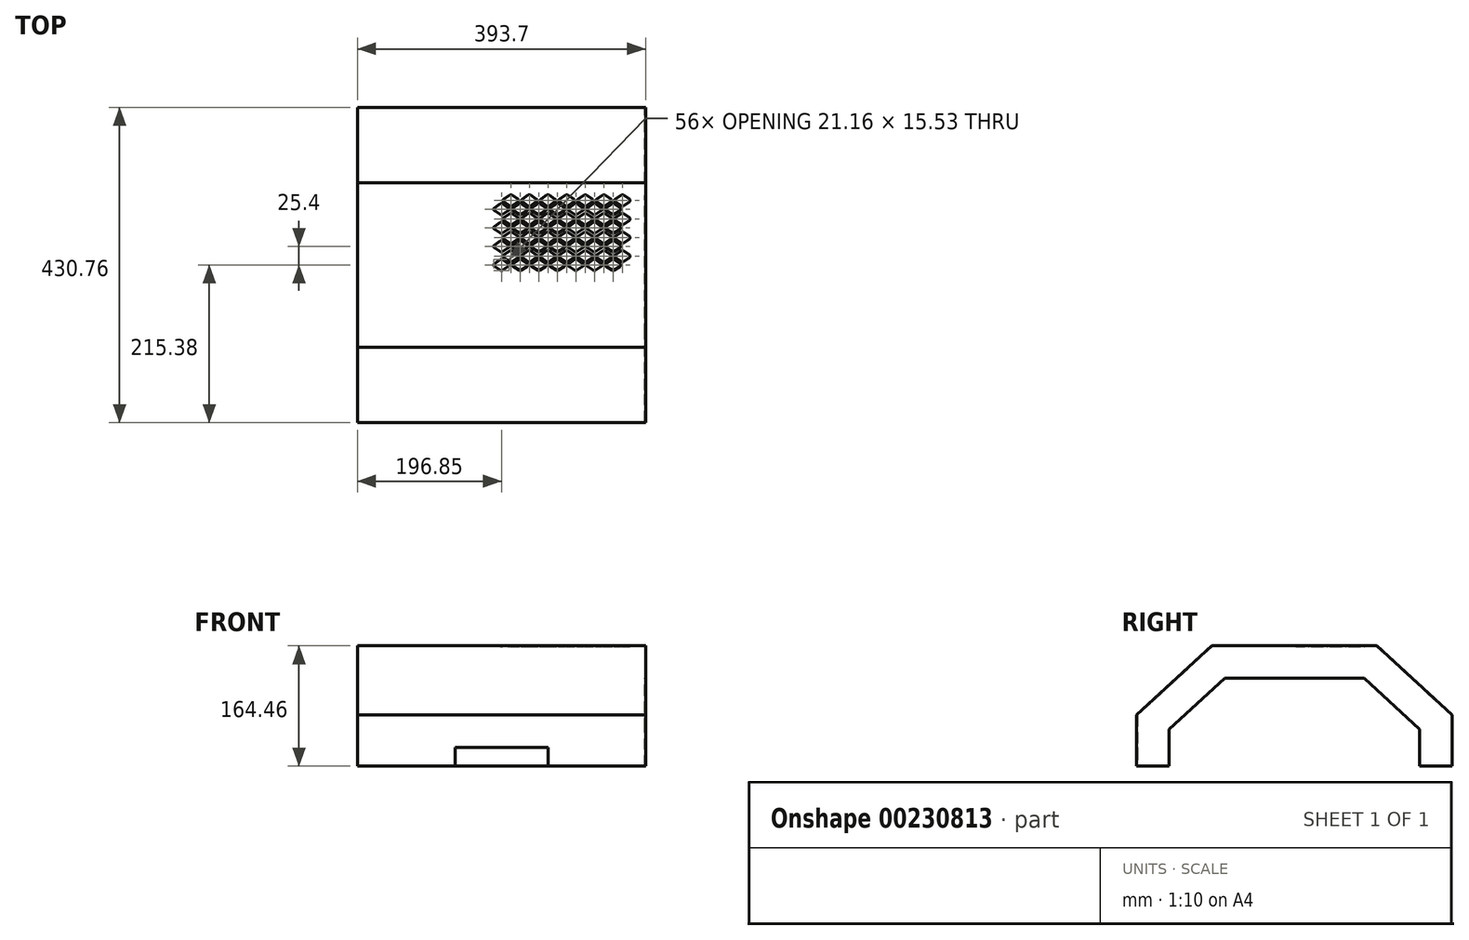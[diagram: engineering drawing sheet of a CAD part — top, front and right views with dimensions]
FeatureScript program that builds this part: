
annotation { "Feature Type Name" : "Feature", "Feature Type Description" : "" }
export const myFeature = defineFeature(function(context is Context, id is Id, definition is map)
    precondition{}
    {
        {
            var Q0;
            Q0=qCreatedBy(makeId("Right.planeOp"),FACE);
            var sketch = newSketch(context, id + "F0", { "sketchPlane" : qUnion([Q0])});
            skLineSegment(sketch, "E0", {"start": v(0, 0) * mm, "end": v(0, 169.27) * mm, "construction": true});
            skLineSegment(sketch, "E1", {"start": v(0, 164.46) * mm, "end": v(112.6, 164.46) * mm});
            skLineSegment(sketch, "E2", {"start": v(112.6, 164.46) * mm, "end": v(215.38, 69.85) * mm});
            skLineSegment(sketch, "E3", {"start": v(215.38, 69.85) * mm, "end": v(215.38, 0) * mm});
            skLineSegment(sketch, "E4", {"start": v(215.38, 0) * mm, "end": v(170.93, 0) * mm});
            skLineSegment(sketch, "E5", {"start": v(170.93, 0) * mm, "end": v(170.93, 50.35) * mm});
            skLineSegment(sketch, "E6", {"start": v(170.93, 50.35) * mm, "end": v(95.25, 120.01) * mm});
            skLineSegment(sketch, "E7", {"start": v(95.25, 120.01) * mm, "end": v(0, 120.01) * mm});
            skLineSegment(sketch, "E8.MirrorCS", {"start": v(0, 164.46) * mm, "end": v(-112.6, 164.46) * mm});
            skLineSegment(sketch, "E9.MirrorCS", {"start": v(-215.38, 0) * mm, "end": v(-170.93, 0) * mm});
            skLineSegment(sketch, "E10.MirrorCS", {"start": v(-170.93, 0) * mm, "end": v(-170.93, 50.35) * mm});
            skLineSegment(sketch, "E11.MirrorCS", {"start": v(-215.38, 69.85) * mm, "end": v(-215.38, 0) * mm});
            skLineSegment(sketch, "E12.MirrorCS", {"start": v(-95.25, 120.01) * mm, "end": v(0, 120.01) * mm});
            skLineSegment(sketch, "E13.MirrorCS", {"start": v(-112.6, 164.46) * mm, "end": v(-215.38, 69.85) * mm});
            skLineSegment(sketch, "E14.MirrorCS", {"start": v(-170.93, 50.35) * mm, "end": v(-95.25, 120.01) * mm});
            skSolve(sketch);
        }
        {
            var Q0;
            Q0=qSketchRegion(id+"F0",true);
            extrude(context, id + "F1", {"entities" : qUnion([Q0]), "endBound" : BoundingType.SYMMETRIC, "depth" : 393.7 * mm});
        }
        {
            var Q0;
            Q0=makeQuery(id+"F1.opExtrude","SWEPT_FACE",FACE,{"disambiguationData":[OSD([sQuery(id+"F0.wireOp",EDGE,"E7"),sQuery(id+"F0.wireOp",EDGE,"E12.MirrorCS")])]});
            var Q1;
            Q1=makeQuery(id+"F1.opExtrude","SWEPT_FACE",FACE,{"disambiguationData":[OSD([sQuery(id+"F0.wireOp",EDGE,"E6")])]});
            var Q2;
            Q2=makeQuery(id+"F1.opExtrude","SWEPT_FACE",FACE,{"disambiguationData":[OSD([sQuery(id+"F0.wireOp",EDGE,"E5")])]});
            var Q3;
            Q3=makeQuery(id+"F1.opExtrude","SWEPT_FACE",FACE,{"disambiguationData":[OSD([sQuery(id+"F0.wireOp",EDGE,"E4")])]});
            var Q4;
            Q4=makeQuery(id+"F1.opExtrude","SWEPT_FACE",FACE,{"disambiguationData":[OSD([sQuery(id+"F0.wireOp",EDGE,"E14.MirrorCS")])]});
            var Q5;
            Q5=makeQuery(id+"F1.opExtrude","SWEPT_FACE",FACE,{"disambiguationData":[OSD([sQuery(id+"F0.wireOp",EDGE,"E10.MirrorCS")])]});
            var Q6;
            Q6=makeQuery(id+"F1.opExtrude","SWEPT_FACE",FACE,{"disambiguationData":[OSD([sQuery(id+"F0.wireOp",EDGE,"E9.MirrorCS")])]});
            shell(context, id + "F2", {"entities" : qUnion([Q0, Q1, Q2, Q3, Q4, Q5, Q6]), "thickness" : 0.95 * mm});
        }
        {
            var Q0;
            Q0=makeQuery(id+"F1.opExtrude","SWEPT_FACE",FACE,{"disambiguationData":[OSD([sQuery(id+"F0.wireOp",EDGE,"E11.MirrorCS")])]});
            var sketch = newSketch(context, id + "F3", { "sketchPlane" : qUnion([Q0])});
            skLineSegment(sketch, "E15.bottom", {"start": v(-63.5, 0) * mm, "end": v(63.5, 0) * mm});
            skLineSegment(sketch, "E15.top", {"start": v(-63.5, 25.4) * mm, "end": v(63.5, 25.4) * mm});
            skLineSegment(sketch, "E15.left", {"start": v(-63.5, 0) * mm, "end": v(-63.5, 25.4) * mm});
            skLineSegment(sketch, "E15.right", {"start": v(63.5, 0) * mm, "end": v(63.5, 25.4) * mm});
            skSolve(sketch);
        }
        {
            var Q0;
            Q0=qSketchRegion(id+"F3",true);
            extrude(context, id + "F4", {"entities" : qUnion([Q0]), "operationType" : NewBodyOperationType.REMOVE, "oppositeDirection" : true, "depth" : 25.4 * mm});
        }
        {
            var Q0;
            Q0=makeQuery(id+"F1.opExtrude","SWEPT_FACE",FACE,{"disambiguationData":[OSD([sQuery(id+"F0.wireOp",EDGE,"E1"),sQuery(id+"F0.wireOp",EDGE,"E8.MirrorCS")])]});
            var sketch = newSketch(context, id + "F5", { "sketchPlane" : qUnion([Q0])});
            skLineSegment(sketch, "E16", {"start": v(-9.42, 2.13) * mm, "end": v(-1.38, 7.36) * mm});
            skLineSegment(sketch, "E17", {"start": v(1.38, 7.36) * mm, "end": v(9.42, 2.13) * mm});
            skLineSegment(sketch, "E18", {"start": v(9.42, -2.13) * mm, "end": v(1.38, -7.36) * mm});
            skLineSegment(sketch, "E19", {"start": v(-1.38, -7.36) * mm, "end": v(-9.42, -2.13) * mm});
            skPoint(sketch, "E20.visualSharp", {"position": v(-12.7, 0) * mm});
            skArc(sketch, "E20.filletArc", {"start": v(-9.42, 2.13) * mm, "mid": v(-10.58, 0) * mm, "end": v(-9.42, -2.13) * mm});
            skPoint(sketch, "E21.visualSharp", {"position": v(0, 8.26) * mm});
            skArc(sketch, "E21.filletArc", {"start": v(1.38, 7.36) * mm, "mid": v(0, 7.77) * mm, "end": v(-1.38, 7.36) * mm});
            skPoint(sketch, "E22.visualSharp", {"position": v(12.7, 0) * mm});
            skArc(sketch, "E22.filletArc", {"start": v(9.42, -2.13) * mm, "mid": v(10.58, 0) * mm, "end": v(9.42, 2.13) * mm});
            skPoint(sketch, "E23.visualSharp", {"position": v(0, -8.26) * mm});
            skArc(sketch, "E23.filletArc", {"start": v(-1.38, -7.36) * mm, "mid": v(0, -7.77) * mm, "end": v(1.38, -7.36) * mm});
            skLineSegment(sketch, "E24.0", {"start": v(3.28, 9.91) * mm, "end": v(11.32, 4.69) * mm});
            skLineSegment(sketch, "E25", {"start": v(3.28, 14.17) * mm, "end": v(11.32, 19.4) * mm});
            skLineSegment(sketch, "E26", {"start": v(14.08, 19.4) * mm, "end": v(22.12, 14.17) * mm});
            skLineSegment(sketch, "E27", {"start": v(22.12, 9.91) * mm, "end": v(14.08, 4.69) * mm});
            skPoint(sketch, "E28.visualSharp", {"position": v(0, 12.04) * mm});
            skArc(sketch, "E28.filletArc", {"start": v(3.28, 14.17) * mm, "mid": v(2.12, 12.04) * mm, "end": v(3.28, 9.91) * mm});
            skPoint(sketch, "E29.visualSharp", {"position": v(12.7, 20.3) * mm});
            skArc(sketch, "E29.filletArc", {"start": v(14.08, 19.4) * mm, "mid": v(12.7, 19.8) * mm, "end": v(11.32, 19.4) * mm});
            skPoint(sketch, "E30.visualSharp", {"position": v(25.4, 12.04) * mm});
            skArc(sketch, "E30.filletArc", {"start": v(22.12, 9.91) * mm, "mid": v(23.28, 12.04) * mm, "end": v(22.12, 14.17) * mm});
            skPoint(sketch, "E31.visualSharp", {"position": v(12.7, 3.79) * mm});
            skArc(sketch, "E31.filletArc", {"start": v(11.32, 4.69) * mm, "mid": v(12.7, 4.28) * mm, "end": v(14.08, 4.69) * mm});
            skPoint(sketch, "E32.0.1.0", {"position": v(25.4, 37.44) * mm});
            skPoint(sketch, "E32.0.1.1", {"position": v(12.7, 45.7) * mm});
            skPoint(sketch, "E32.0.1.2", {"position": v(0, 33.66) * mm});
            skPoint(sketch, "E32.0.1.3", {"position": v(-12.7, 25.4) * mm});
            skPoint(sketch, "E32.0.1.4", {"position": v(0, 17.14) * mm});
            skPoint(sketch, "E32.0.1.5", {"position": v(12.7, 25.4) * mm});
            skPoint(sketch, "E32.0.1.6", {"position": v(0, 37.44) * mm});
            skPoint(sketch, "E32.0.1.7", {"position": v(12.7, 29.19) * mm});
            skArc(sketch, "E32.0.1.8", {"start": v(-9.42, 27.53) * mm, "mid": v(-10.58, 25.4) * mm, "end": v(-9.42, 23.27) * mm});
            skLineSegment(sketch, "E32.0.1.9", {"start": v(14.08, 44.8) * mm, "end": v(22.12, 39.57) * mm});
            skArc(sketch, "E32.0.1.10", {"start": v(9.42, 23.27) * mm, "mid": v(10.58, 25.4) * mm, "end": v(9.42, 27.53) * mm});
            skArc(sketch, "E32.0.1.11", {"start": v(3.28, 39.57) * mm, "mid": v(2.12, 37.44) * mm, "end": v(3.28, 35.31) * mm});
            skLineSegment(sketch, "E32.0.1.12", {"start": v(3.28, 39.57) * mm, "end": v(11.32, 44.8) * mm});
            skLineSegment(sketch, "E32.0.1.13", {"start": v(9.42, 23.27) * mm, "end": v(1.38, 18.04) * mm});
            skLineSegment(sketch, "E32.0.1.14", {"start": v(-1.38, 18.04) * mm, "end": v(-9.42, 23.27) * mm});
            skLineSegment(sketch, "E32.0.1.15", {"start": v(-9.42, 27.53) * mm, "end": v(-1.38, 32.76) * mm});
            skArc(sketch, "E32.0.1.16", {"start": v(14.08, 44.8) * mm, "mid": v(12.7, 45.2) * mm, "end": v(11.32, 44.8) * mm});
            skArc(sketch, "E32.0.1.17", {"start": v(22.12, 35.31) * mm, "mid": v(23.28, 37.44) * mm, "end": v(22.12, 39.57) * mm});
            skLineSegment(sketch, "E32.0.1.18", {"start": v(22.12, 35.31) * mm, "end": v(14.08, 30.09) * mm});
            skArc(sketch, "E32.0.1.19", {"start": v(-1.38, 18.04) * mm, "mid": v(0, 17.63) * mm, "end": v(1.38, 18.04) * mm});
            skArc(sketch, "E32.0.1.20", {"start": v(1.38, 32.76) * mm, "mid": v(0, 33.17) * mm, "end": v(-1.38, 32.76) * mm});
            skLineSegment(sketch, "E32.0.1.21", {"start": v(3.28, 35.31) * mm, "end": v(11.32, 30.09) * mm});
            skLineSegment(sketch, "E32.0.1.22", {"start": v(1.38, 32.76) * mm, "end": v(9.42, 27.53) * mm});
            skArc(sketch, "E32.0.1.23", {"start": v(11.32, 30.09) * mm, "mid": v(12.7, 29.68) * mm, "end": v(14.08, 30.09) * mm});
            skPoint(sketch, "E32.0.2.0", {"position": v(25.4, 62.84) * mm});
            skPoint(sketch, "E32.0.2.1", {"position": v(12.7, 71.1) * mm});
            skPoint(sketch, "E32.0.2.2", {"position": v(0, 59.06) * mm});
            skPoint(sketch, "E32.0.2.3", {"position": v(-12.7, 50.8) * mm});
            skPoint(sketch, "E32.0.2.4", {"position": v(0, 42.55) * mm});
            skPoint(sketch, "E32.0.2.5", {"position": v(12.7, 50.8) * mm});
            skPoint(sketch, "E32.0.2.6", {"position": v(0, 62.84) * mm});
            skPoint(sketch, "E32.0.2.7", {"position": v(12.7, 54.59) * mm});
            skArc(sketch, "E32.0.2.8", {"start": v(-9.42, 52.93) * mm, "mid": v(-10.58, 50.8) * mm, "end": v(-9.42, 48.67) * mm});
            skLineSegment(sketch, "E32.0.2.9", {"start": v(14.08, 70.2) * mm, "end": v(22.12, 64.97) * mm});
            skArc(sketch, "E32.0.2.10", {"start": v(9.42, 48.67) * mm, "mid": v(10.58, 50.8) * mm, "end": v(9.42, 52.93) * mm});
            skArc(sketch, "E32.0.2.11", {"start": v(3.28, 64.97) * mm, "mid": v(2.12, 62.84) * mm, "end": v(3.28, 60.71) * mm});
            skLineSegment(sketch, "E32.0.2.12", {"start": v(3.28, 64.97) * mm, "end": v(11.32, 70.2) * mm});
            skLineSegment(sketch, "E32.0.2.13", {"start": v(9.42, 48.67) * mm, "end": v(1.38, 43.44) * mm});
            skLineSegment(sketch, "E32.0.2.14", {"start": v(-1.38, 43.44) * mm, "end": v(-9.42, 48.67) * mm});
            skLineSegment(sketch, "E32.0.2.15", {"start": v(-9.42, 52.93) * mm, "end": v(-1.38, 58.16) * mm});
            skArc(sketch, "E32.0.2.16", {"start": v(14.08, 70.2) * mm, "mid": v(12.7, 70.6) * mm, "end": v(11.32, 70.2) * mm});
            skArc(sketch, "E32.0.2.17", {"start": v(22.12, 60.71) * mm, "mid": v(23.28, 62.84) * mm, "end": v(22.12, 64.97) * mm});
            skLineSegment(sketch, "E32.0.2.18", {"start": v(22.12, 60.71) * mm, "end": v(14.08, 55.49) * mm});
            skArc(sketch, "E32.0.2.19", {"start": v(-1.38, 43.44) * mm, "mid": v(0, 43.03) * mm, "end": v(1.38, 43.44) * mm});
            skArc(sketch, "E32.0.2.20", {"start": v(1.38, 58.16) * mm, "mid": v(0, 58.57) * mm, "end": v(-1.38, 58.16) * mm});
            skLineSegment(sketch, "E32.0.2.21", {"start": v(3.28, 60.71) * mm, "end": v(11.32, 55.49) * mm});
            skLineSegment(sketch, "E32.0.2.22", {"start": v(1.38, 58.16) * mm, "end": v(9.42, 52.93) * mm});
            skArc(sketch, "E32.0.2.23", {"start": v(11.32, 55.49) * mm, "mid": v(12.7, 55.08) * mm, "end": v(14.08, 55.49) * mm});
            skPoint(sketch, "E32.0.3.0", {"position": v(25.4, 88.24) * mm});
            skPoint(sketch, "E32.0.3.1", {"position": v(12.7, 96.5) * mm});
            skPoint(sketch, "E32.0.3.2", {"position": v(0, 84.45) * mm});
            skPoint(sketch, "E32.0.3.3", {"position": v(-12.7, 76.2) * mm});
            skPoint(sketch, "E32.0.3.4", {"position": v(0, 67.94) * mm});
            skPoint(sketch, "E32.0.3.5", {"position": v(12.7, 76.2) * mm});
            skPoint(sketch, "E32.0.3.6", {"position": v(0, 88.24) * mm});
            skPoint(sketch, "E32.0.3.7", {"position": v(12.7, 79.99) * mm});
            skArc(sketch, "E32.0.3.8", {"start": v(-9.42, 78.33) * mm, "mid": v(-10.58, 76.2) * mm, "end": v(-9.42, 74.07) * mm});
            skLineSegment(sketch, "E32.0.3.9", {"start": v(14.08, 95.6) * mm, "end": v(22.12, 90.37) * mm});
            skArc(sketch, "E32.0.3.10", {"start": v(9.42, 74.07) * mm, "mid": v(10.58, 76.2) * mm, "end": v(9.42, 78.33) * mm});
            skArc(sketch, "E32.0.3.11", {"start": v(3.28, 90.37) * mm, "mid": v(2.12, 88.24) * mm, "end": v(3.28, 86.11) * mm});
            skLineSegment(sketch, "E32.0.3.12", {"start": v(3.28, 90.37) * mm, "end": v(11.32, 95.6) * mm});
            skLineSegment(sketch, "E32.0.3.13", {"start": v(9.42, 74.07) * mm, "end": v(1.38, 68.84) * mm});
            skLineSegment(sketch, "E32.0.3.14", {"start": v(-1.38, 68.84) * mm, "end": v(-9.42, 74.07) * mm});
            skLineSegment(sketch, "E32.0.3.15", {"start": v(-9.42, 78.33) * mm, "end": v(-1.38, 83.56) * mm});
            skArc(sketch, "E32.0.3.16", {"start": v(14.08, 95.6) * mm, "mid": v(12.7, 96) * mm, "end": v(11.32, 95.6) * mm});
            skArc(sketch, "E32.0.3.17", {"start": v(22.12, 86.11) * mm, "mid": v(23.28, 88.24) * mm, "end": v(22.12, 90.37) * mm});
            skLineSegment(sketch, "E32.0.3.18", {"start": v(22.12, 86.11) * mm, "end": v(14.08, 80.89) * mm});
            skArc(sketch, "E32.0.3.19", {"start": v(-1.38, 68.84) * mm, "mid": v(0, 68.43) * mm, "end": v(1.38, 68.84) * mm});
            skArc(sketch, "E32.0.3.20", {"start": v(1.38, 83.56) * mm, "mid": v(0, 83.97) * mm, "end": v(-1.38, 83.56) * mm});
            skLineSegment(sketch, "E32.0.3.21", {"start": v(3.28, 86.11) * mm, "end": v(11.32, 80.89) * mm});
            skLineSegment(sketch, "E32.0.3.22", {"start": v(1.38, 83.56) * mm, "end": v(9.42, 78.33) * mm});
            skArc(sketch, "E32.0.3.23", {"start": v(11.32, 80.89) * mm, "mid": v(12.7, 80.48) * mm, "end": v(14.08, 80.89) * mm});
            skPoint(sketch, "E32.1.0.0", {"position": v(50.8, 12.04) * mm});
            skPoint(sketch, "E32.1.0.1", {"position": v(38.1, 20.3) * mm});
            skPoint(sketch, "E32.1.0.2", {"position": v(25.4, 8.26) * mm});
            skPoint(sketch, "E32.1.0.4", {"position": v(25.4, -8.26) * mm});
            skPoint(sketch, "E32.1.0.5", {"position": v(38.1, 0) * mm});
            skPoint(sketch, "E32.1.0.7", {"position": v(38.1, 3.79) * mm});
            skArc(sketch, "E32.1.0.8", {"start": v(15.98, 2.13) * mm, "mid": v(14.82, 0) * mm, "end": v(15.98, -2.13) * mm});
            skLineSegment(sketch, "E32.1.0.9", {"start": v(39.48, 19.4) * mm, "end": v(47.52, 14.17) * mm});
            skArc(sketch, "E32.1.0.10", {"start": v(34.82, -2.13) * mm, "mid": v(35.98, 0) * mm, "end": v(34.82, 2.13) * mm});
            skArc(sketch, "E32.1.0.11", {"start": v(28.68, 14.17) * mm, "mid": v(27.52, 12.04) * mm, "end": v(28.68, 9.91) * mm});
            skLineSegment(sketch, "E32.1.0.12", {"start": v(28.68, 14.17) * mm, "end": v(36.72, 19.4) * mm});
            skLineSegment(sketch, "E32.1.0.13", {"start": v(34.82, -2.13) * mm, "end": v(26.78, -7.36) * mm});
            skLineSegment(sketch, "E32.1.0.14", {"start": v(24.02, -7.36) * mm, "end": v(15.98, -2.13) * mm});
            skLineSegment(sketch, "E32.1.0.15", {"start": v(15.98, 2.13) * mm, "end": v(24.02, 7.36) * mm});
            skArc(sketch, "E32.1.0.16", {"start": v(39.48, 19.4) * mm, "mid": v(38.1, 19.8) * mm, "end": v(36.72, 19.4) * mm});
            skArc(sketch, "E32.1.0.17", {"start": v(47.52, 9.91) * mm, "mid": v(48.68, 12.04) * mm, "end": v(47.52, 14.17) * mm});
            skLineSegment(sketch, "E32.1.0.18", {"start": v(47.52, 9.91) * mm, "end": v(39.48, 4.69) * mm});
            skArc(sketch, "E32.1.0.19", {"start": v(24.02, -7.36) * mm, "mid": v(25.4, -7.77) * mm, "end": v(26.78, -7.36) * mm});
            skArc(sketch, "E32.1.0.20", {"start": v(26.78, 7.36) * mm, "mid": v(25.4, 7.77) * mm, "end": v(24.02, 7.36) * mm});
            skLineSegment(sketch, "E32.1.0.21", {"start": v(28.68, 9.91) * mm, "end": v(36.72, 4.69) * mm});
            skLineSegment(sketch, "E32.1.0.22", {"start": v(26.78, 7.36) * mm, "end": v(34.82, 2.13) * mm});
            skArc(sketch, "E32.1.0.23", {"start": v(36.72, 4.69) * mm, "mid": v(38.1, 4.28) * mm, "end": v(39.48, 4.69) * mm});
            skPoint(sketch, "E32.1.1.0", {"position": v(50.8, 37.44) * mm});
            skPoint(sketch, "E32.1.1.1", {"position": v(38.1, 45.7) * mm});
            skPoint(sketch, "E32.1.1.2", {"position": v(25.4, 33.66) * mm});
            skPoint(sketch, "E32.1.1.3", {"position": v(12.7, 25.4) * mm});
            skPoint(sketch, "E32.1.1.4", {"position": v(25.4, 17.14) * mm});
            skPoint(sketch, "E32.1.1.5", {"position": v(38.1, 25.4) * mm});
            skPoint(sketch, "E32.1.1.6", {"position": v(25.4, 37.44) * mm});
            skPoint(sketch, "E32.1.1.7", {"position": v(38.1, 29.19) * mm});
            skArc(sketch, "E32.1.1.8", {"start": v(15.98, 27.53) * mm, "mid": v(14.82, 25.4) * mm, "end": v(15.98, 23.27) * mm});
            skLineSegment(sketch, "E32.1.1.9", {"start": v(39.48, 44.8) * mm, "end": v(47.52, 39.57) * mm});
            skArc(sketch, "E32.1.1.10", {"start": v(34.82, 23.27) * mm, "mid": v(35.98, 25.4) * mm, "end": v(34.82, 27.53) * mm});
            skArc(sketch, "E32.1.1.11", {"start": v(28.68, 39.57) * mm, "mid": v(27.52, 37.44) * mm, "end": v(28.68, 35.31) * mm});
            skLineSegment(sketch, "E32.1.1.12", {"start": v(28.68, 39.57) * mm, "end": v(36.72, 44.8) * mm});
            skLineSegment(sketch, "E32.1.1.13", {"start": v(34.82, 23.27) * mm, "end": v(26.78, 18.04) * mm});
            skLineSegment(sketch, "E32.1.1.14", {"start": v(24.02, 18.04) * mm, "end": v(15.98, 23.27) * mm});
            skLineSegment(sketch, "E32.1.1.15", {"start": v(15.98, 27.53) * mm, "end": v(24.02, 32.76) * mm});
            skArc(sketch, "E32.1.1.16", {"start": v(39.48, 44.8) * mm, "mid": v(38.1, 45.2) * mm, "end": v(36.72, 44.8) * mm});
            skArc(sketch, "E32.1.1.17", {"start": v(47.52, 35.31) * mm, "mid": v(48.68, 37.44) * mm, "end": v(47.52, 39.57) * mm});
            skLineSegment(sketch, "E32.1.1.18", {"start": v(47.52, 35.31) * mm, "end": v(39.48, 30.09) * mm});
            skArc(sketch, "E32.1.1.19", {"start": v(24.02, 18.04) * mm, "mid": v(25.4, 17.63) * mm, "end": v(26.78, 18.04) * mm});
            skArc(sketch, "E32.1.1.20", {"start": v(26.78, 32.76) * mm, "mid": v(25.4, 33.17) * mm, "end": v(24.02, 32.76) * mm});
            skLineSegment(sketch, "E32.1.1.21", {"start": v(28.68, 35.31) * mm, "end": v(36.72, 30.09) * mm});
            skLineSegment(sketch, "E32.1.1.22", {"start": v(26.78, 32.76) * mm, "end": v(34.82, 27.53) * mm});
            skArc(sketch, "E32.1.1.23", {"start": v(36.72, 30.09) * mm, "mid": v(38.1, 29.68) * mm, "end": v(39.48, 30.09) * mm});
            skPoint(sketch, "E32.1.2.0", {"position": v(50.8, 62.84) * mm});
            skPoint(sketch, "E32.1.2.1", {"position": v(38.1, 71.1) * mm});
            skPoint(sketch, "E32.1.2.2", {"position": v(25.4, 59.06) * mm});
            skPoint(sketch, "E32.1.2.3", {"position": v(12.7, 50.8) * mm});
            skPoint(sketch, "E32.1.2.4", {"position": v(25.4, 42.55) * mm});
            skPoint(sketch, "E32.1.2.5", {"position": v(38.1, 50.8) * mm});
            skPoint(sketch, "E32.1.2.6", {"position": v(25.4, 62.84) * mm});
            skPoint(sketch, "E32.1.2.7", {"position": v(38.1, 54.59) * mm});
            skArc(sketch, "E32.1.2.8", {"start": v(15.98, 52.93) * mm, "mid": v(14.82, 50.8) * mm, "end": v(15.98, 48.67) * mm});
            skLineSegment(sketch, "E32.1.2.9", {"start": v(39.48, 70.2) * mm, "end": v(47.52, 64.97) * mm});
            skArc(sketch, "E32.1.2.10", {"start": v(34.82, 48.67) * mm, "mid": v(35.98, 50.8) * mm, "end": v(34.82, 52.93) * mm});
            skArc(sketch, "E32.1.2.11", {"start": v(28.68, 64.97) * mm, "mid": v(27.52, 62.84) * mm, "end": v(28.68, 60.71) * mm});
            skLineSegment(sketch, "E32.1.2.12", {"start": v(28.68, 64.97) * mm, "end": v(36.72, 70.2) * mm});
            skLineSegment(sketch, "E32.1.2.13", {"start": v(34.82, 48.67) * mm, "end": v(26.78, 43.44) * mm});
            skLineSegment(sketch, "E32.1.2.14", {"start": v(24.02, 43.44) * mm, "end": v(15.98, 48.67) * mm});
            skLineSegment(sketch, "E32.1.2.15", {"start": v(15.98, 52.93) * mm, "end": v(24.02, 58.16) * mm});
            skArc(sketch, "E32.1.2.16", {"start": v(39.48, 70.2) * mm, "mid": v(38.1, 70.6) * mm, "end": v(36.72, 70.2) * mm});
            skArc(sketch, "E32.1.2.17", {"start": v(47.52, 60.71) * mm, "mid": v(48.68, 62.84) * mm, "end": v(47.52, 64.97) * mm});
            skLineSegment(sketch, "E32.1.2.18", {"start": v(47.52, 60.71) * mm, "end": v(39.48, 55.49) * mm});
            skArc(sketch, "E32.1.2.19", {"start": v(24.02, 43.44) * mm, "mid": v(25.4, 43.03) * mm, "end": v(26.78, 43.44) * mm});
            skArc(sketch, "E32.1.2.20", {"start": v(26.78, 58.16) * mm, "mid": v(25.4, 58.57) * mm, "end": v(24.02, 58.16) * mm});
            skLineSegment(sketch, "E32.1.2.21", {"start": v(28.68, 60.71) * mm, "end": v(36.72, 55.49) * mm});
            skLineSegment(sketch, "E32.1.2.22", {"start": v(26.78, 58.16) * mm, "end": v(34.82, 52.93) * mm});
            skArc(sketch, "E32.1.2.23", {"start": v(36.72, 55.49) * mm, "mid": v(38.1, 55.08) * mm, "end": v(39.48, 55.49) * mm});
            skPoint(sketch, "E32.1.3.0", {"position": v(50.8, 88.24) * mm});
            skPoint(sketch, "E32.1.3.1", {"position": v(38.1, 96.5) * mm});
            skPoint(sketch, "E32.1.3.2", {"position": v(25.4, 84.45) * mm});
            skPoint(sketch, "E32.1.3.3", {"position": v(12.7, 76.2) * mm});
            skPoint(sketch, "E32.1.3.4", {"position": v(25.4, 67.94) * mm});
            skPoint(sketch, "E32.1.3.5", {"position": v(38.1, 76.2) * mm});
            skPoint(sketch, "E32.1.3.6", {"position": v(25.4, 88.24) * mm});
            skPoint(sketch, "E32.1.3.7", {"position": v(38.1, 79.99) * mm});
            skArc(sketch, "E32.1.3.8", {"start": v(15.98, 78.33) * mm, "mid": v(14.82, 76.2) * mm, "end": v(15.98, 74.07) * mm});
            skLineSegment(sketch, "E32.1.3.9", {"start": v(39.48, 95.6) * mm, "end": v(47.52, 90.37) * mm});
            skArc(sketch, "E32.1.3.10", {"start": v(34.82, 74.07) * mm, "mid": v(35.98, 76.2) * mm, "end": v(34.82, 78.33) * mm});
            skArc(sketch, "E32.1.3.11", {"start": v(28.68, 90.37) * mm, "mid": v(27.52, 88.24) * mm, "end": v(28.68, 86.11) * mm});
            skLineSegment(sketch, "E32.1.3.12", {"start": v(28.68, 90.37) * mm, "end": v(36.72, 95.6) * mm});
            skLineSegment(sketch, "E32.1.3.13", {"start": v(34.82, 74.07) * mm, "end": v(26.78, 68.84) * mm});
            skLineSegment(sketch, "E32.1.3.14", {"start": v(24.02, 68.84) * mm, "end": v(15.98, 74.07) * mm});
            skLineSegment(sketch, "E32.1.3.15", {"start": v(15.98, 78.33) * mm, "end": v(24.02, 83.56) * mm});
            skArc(sketch, "E32.1.3.16", {"start": v(39.48, 95.6) * mm, "mid": v(38.1, 96) * mm, "end": v(36.72, 95.6) * mm});
            skArc(sketch, "E32.1.3.17", {"start": v(47.52, 86.11) * mm, "mid": v(48.68, 88.24) * mm, "end": v(47.52, 90.37) * mm});
            skLineSegment(sketch, "E32.1.3.18", {"start": v(47.52, 86.11) * mm, "end": v(39.48, 80.89) * mm});
            skArc(sketch, "E32.1.3.19", {"start": v(24.02, 68.84) * mm, "mid": v(25.4, 68.43) * mm, "end": v(26.78, 68.84) * mm});
            skArc(sketch, "E32.1.3.20", {"start": v(26.78, 83.56) * mm, "mid": v(25.4, 83.97) * mm, "end": v(24.02, 83.56) * mm});
            skLineSegment(sketch, "E32.1.3.21", {"start": v(28.68, 86.11) * mm, "end": v(36.72, 80.89) * mm});
            skLineSegment(sketch, "E32.1.3.22", {"start": v(26.78, 83.56) * mm, "end": v(34.82, 78.33) * mm});
            skArc(sketch, "E32.1.3.23", {"start": v(36.72, 80.89) * mm, "mid": v(38.1, 80.48) * mm, "end": v(39.48, 80.89) * mm});
            skPoint(sketch, "E32.2.0.0", {"position": v(76.2, 12.04) * mm});
            skPoint(sketch, "E32.2.0.1", {"position": v(63.5, 20.3) * mm});
            skPoint(sketch, "E32.2.0.2", {"position": v(50.8, 8.26) * mm});
            skPoint(sketch, "E32.2.0.3", {"position": v(38.1, 0) * mm});
            skPoint(sketch, "E32.2.0.4", {"position": v(50.8, -8.26) * mm});
            skPoint(sketch, "E32.2.0.5", {"position": v(63.5, 0) * mm});
            skPoint(sketch, "E32.2.0.6", {"position": v(50.8, 12.04) * mm});
            skPoint(sketch, "E32.2.0.7", {"position": v(63.5, 3.79) * mm});
            skArc(sketch, "E32.2.0.8", {"start": v(41.38, 2.13) * mm, "mid": v(40.22, 0) * mm, "end": v(41.38, -2.13) * mm});
            skLineSegment(sketch, "E32.2.0.9", {"start": v(64.88, 19.4) * mm, "end": v(72.92, 14.17) * mm});
            skArc(sketch, "E32.2.0.10", {"start": v(60.22, -2.13) * mm, "mid": v(61.38, 0) * mm, "end": v(60.22, 2.13) * mm});
            skArc(sketch, "E32.2.0.11", {"start": v(54.08, 14.17) * mm, "mid": v(52.92, 12.04) * mm, "end": v(54.08, 9.91) * mm});
            skLineSegment(sketch, "E32.2.0.12", {"start": v(54.08, 14.17) * mm, "end": v(62.12, 19.4) * mm});
            skLineSegment(sketch, "E32.2.0.13", {"start": v(60.22, -2.13) * mm, "end": v(52.18, -7.36) * mm});
            skLineSegment(sketch, "E32.2.0.14", {"start": v(49.42, -7.36) * mm, "end": v(41.38, -2.13) * mm});
            skLineSegment(sketch, "E32.2.0.15", {"start": v(41.38, 2.13) * mm, "end": v(49.42, 7.36) * mm});
            skArc(sketch, "E32.2.0.16", {"start": v(64.88, 19.4) * mm, "mid": v(63.5, 19.8) * mm, "end": v(62.12, 19.4) * mm});
            skArc(sketch, "E32.2.0.17", {"start": v(72.92, 9.91) * mm, "mid": v(74.08, 12.04) * mm, "end": v(72.92, 14.17) * mm});
            skLineSegment(sketch, "E32.2.0.18", {"start": v(72.92, 9.91) * mm, "end": v(64.88, 4.69) * mm});
            skArc(sketch, "E32.2.0.19", {"start": v(49.42, -7.36) * mm, "mid": v(50.8, -7.77) * mm, "end": v(52.18, -7.36) * mm});
            skArc(sketch, "E32.2.0.20", {"start": v(52.18, 7.36) * mm, "mid": v(50.8, 7.77) * mm, "end": v(49.42, 7.36) * mm});
            skLineSegment(sketch, "E32.2.0.21", {"start": v(54.08, 9.91) * mm, "end": v(62.12, 4.69) * mm});
            skLineSegment(sketch, "E32.2.0.22", {"start": v(52.18, 7.36) * mm, "end": v(60.22, 2.13) * mm});
            skArc(sketch, "E32.2.0.23", {"start": v(62.12, 4.69) * mm, "mid": v(63.5, 4.28) * mm, "end": v(64.88, 4.69) * mm});
            skPoint(sketch, "E32.2.1.0", {"position": v(76.2, 37.44) * mm});
            skPoint(sketch, "E32.2.1.1", {"position": v(63.5, 45.7) * mm});
            skPoint(sketch, "E32.2.1.2", {"position": v(50.8, 33.66) * mm});
            skPoint(sketch, "E32.2.1.3", {"position": v(38.1, 25.4) * mm});
            skPoint(sketch, "E32.2.1.4", {"position": v(50.8, 17.14) * mm});
            skPoint(sketch, "E32.2.1.5", {"position": v(63.5, 25.4) * mm});
            skPoint(sketch, "E32.2.1.6", {"position": v(50.8, 37.44) * mm});
            skPoint(sketch, "E32.2.1.7", {"position": v(63.5, 29.19) * mm});
            skArc(sketch, "E32.2.1.8", {"start": v(41.38, 27.53) * mm, "mid": v(40.22, 25.4) * mm, "end": v(41.38, 23.27) * mm});
            skLineSegment(sketch, "E32.2.1.9", {"start": v(64.88, 44.8) * mm, "end": v(72.92, 39.57) * mm});
            skArc(sketch, "E32.2.1.10", {"start": v(60.22, 23.27) * mm, "mid": v(61.38, 25.4) * mm, "end": v(60.22, 27.53) * mm});
            skArc(sketch, "E32.2.1.11", {"start": v(54.08, 39.57) * mm, "mid": v(52.92, 37.44) * mm, "end": v(54.08, 35.31) * mm});
            skLineSegment(sketch, "E32.2.1.12", {"start": v(54.08, 39.57) * mm, "end": v(62.12, 44.8) * mm});
            skLineSegment(sketch, "E32.2.1.13", {"start": v(60.22, 23.27) * mm, "end": v(52.18, 18.04) * mm});
            skLineSegment(sketch, "E32.2.1.14", {"start": v(49.42, 18.04) * mm, "end": v(41.38, 23.27) * mm});
            skLineSegment(sketch, "E32.2.1.15", {"start": v(41.38, 27.53) * mm, "end": v(49.42, 32.76) * mm});
            skArc(sketch, "E32.2.1.16", {"start": v(64.88, 44.8) * mm, "mid": v(63.5, 45.2) * mm, "end": v(62.12, 44.8) * mm});
            skArc(sketch, "E32.2.1.17", {"start": v(72.92, 35.31) * mm, "mid": v(74.08, 37.44) * mm, "end": v(72.92, 39.57) * mm});
            skLineSegment(sketch, "E32.2.1.18", {"start": v(72.92, 35.31) * mm, "end": v(64.88, 30.09) * mm});
            skArc(sketch, "E32.2.1.19", {"start": v(49.42, 18.04) * mm, "mid": v(50.8, 17.63) * mm, "end": v(52.18, 18.04) * mm});
            skArc(sketch, "E32.2.1.20", {"start": v(52.18, 32.76) * mm, "mid": v(50.8, 33.17) * mm, "end": v(49.42, 32.76) * mm});
            skLineSegment(sketch, "E32.2.1.21", {"start": v(54.08, 35.31) * mm, "end": v(62.12, 30.09) * mm});
            skLineSegment(sketch, "E32.2.1.22", {"start": v(52.18, 32.76) * mm, "end": v(60.22, 27.53) * mm});
            skArc(sketch, "E32.2.1.23", {"start": v(62.12, 30.09) * mm, "mid": v(63.5, 29.68) * mm, "end": v(64.88, 30.09) * mm});
            skPoint(sketch, "E32.2.2.0", {"position": v(76.2, 62.84) * mm});
            skPoint(sketch, "E32.2.2.1", {"position": v(63.5, 71.1) * mm});
            skPoint(sketch, "E32.2.2.2", {"position": v(50.8, 59.06) * mm});
            skPoint(sketch, "E32.2.2.3", {"position": v(38.1, 50.8) * mm});
            skPoint(sketch, "E32.2.2.4", {"position": v(50.8, 42.55) * mm});
            skPoint(sketch, "E32.2.2.5", {"position": v(63.5, 50.8) * mm});
            skPoint(sketch, "E32.2.2.6", {"position": v(50.8, 62.84) * mm});
            skPoint(sketch, "E32.2.2.7", {"position": v(63.5, 54.59) * mm});
            skArc(sketch, "E32.2.2.8", {"start": v(41.38, 52.93) * mm, "mid": v(40.22, 50.8) * mm, "end": v(41.38, 48.67) * mm});
            skLineSegment(sketch, "E32.2.2.9", {"start": v(64.88, 70.2) * mm, "end": v(72.92, 64.97) * mm});
            skArc(sketch, "E32.2.2.10", {"start": v(60.22, 48.67) * mm, "mid": v(61.38, 50.8) * mm, "end": v(60.22, 52.93) * mm});
            skArc(sketch, "E32.2.2.11", {"start": v(54.08, 64.97) * mm, "mid": v(52.92, 62.84) * mm, "end": v(54.08, 60.71) * mm});
            skLineSegment(sketch, "E32.2.2.12", {"start": v(54.08, 64.97) * mm, "end": v(62.12, 70.2) * mm});
            skLineSegment(sketch, "E32.2.2.13", {"start": v(60.22, 48.67) * mm, "end": v(52.18, 43.44) * mm});
            skLineSegment(sketch, "E32.2.2.14", {"start": v(49.42, 43.44) * mm, "end": v(41.38, 48.67) * mm});
            skLineSegment(sketch, "E32.2.2.15", {"start": v(41.38, 52.93) * mm, "end": v(49.42, 58.16) * mm});
            skArc(sketch, "E32.2.2.16", {"start": v(64.88, 70.2) * mm, "mid": v(63.5, 70.6) * mm, "end": v(62.12, 70.2) * mm});
            skArc(sketch, "E32.2.2.17", {"start": v(72.92, 60.71) * mm, "mid": v(74.08, 62.84) * mm, "end": v(72.92, 64.97) * mm});
            skLineSegment(sketch, "E32.2.2.18", {"start": v(72.92, 60.71) * mm, "end": v(64.88, 55.49) * mm});
            skArc(sketch, "E32.2.2.19", {"start": v(49.42, 43.44) * mm, "mid": v(50.8, 43.03) * mm, "end": v(52.18, 43.44) * mm});
            skArc(sketch, "E32.2.2.20", {"start": v(52.18, 58.16) * mm, "mid": v(50.8, 58.57) * mm, "end": v(49.42, 58.16) * mm});
            skLineSegment(sketch, "E32.2.2.21", {"start": v(54.08, 60.71) * mm, "end": v(62.12, 55.49) * mm});
            skLineSegment(sketch, "E32.2.2.22", {"start": v(52.18, 58.16) * mm, "end": v(60.22, 52.93) * mm});
            skArc(sketch, "E32.2.2.23", {"start": v(62.12, 55.49) * mm, "mid": v(63.5, 55.08) * mm, "end": v(64.88, 55.49) * mm});
            skPoint(sketch, "E32.2.3.0", {"position": v(76.2, 88.24) * mm});
            skPoint(sketch, "E32.2.3.1", {"position": v(63.5, 96.5) * mm});
            skPoint(sketch, "E32.2.3.2", {"position": v(50.8, 84.45) * mm});
            skPoint(sketch, "E32.2.3.3", {"position": v(38.1, 76.2) * mm});
            skPoint(sketch, "E32.2.3.4", {"position": v(50.8, 67.94) * mm});
            skPoint(sketch, "E32.2.3.5", {"position": v(63.5, 76.2) * mm});
            skPoint(sketch, "E32.2.3.6", {"position": v(50.8, 88.24) * mm});
            skPoint(sketch, "E32.2.3.7", {"position": v(63.5, 79.99) * mm});
            skArc(sketch, "E32.2.3.8", {"start": v(41.38, 78.33) * mm, "mid": v(40.22, 76.2) * mm, "end": v(41.38, 74.07) * mm});
            skLineSegment(sketch, "E32.2.3.9", {"start": v(64.88, 95.6) * mm, "end": v(72.92, 90.37) * mm});
            skArc(sketch, "E32.2.3.10", {"start": v(60.22, 74.07) * mm, "mid": v(61.38, 76.2) * mm, "end": v(60.22, 78.33) * mm});
            skArc(sketch, "E32.2.3.11", {"start": v(54.08, 90.37) * mm, "mid": v(52.92, 88.24) * mm, "end": v(54.08, 86.11) * mm});
            skLineSegment(sketch, "E32.2.3.12", {"start": v(54.08, 90.37) * mm, "end": v(62.12, 95.6) * mm});
            skLineSegment(sketch, "E32.2.3.13", {"start": v(60.22, 74.07) * mm, "end": v(52.18, 68.84) * mm});
            skLineSegment(sketch, "E32.2.3.14", {"start": v(49.42, 68.84) * mm, "end": v(41.38, 74.07) * mm});
            skLineSegment(sketch, "E32.2.3.15", {"start": v(41.38, 78.33) * mm, "end": v(49.42, 83.56) * mm});
            skArc(sketch, "E32.2.3.16", {"start": v(64.88, 95.6) * mm, "mid": v(63.5, 96) * mm, "end": v(62.12, 95.6) * mm});
            skArc(sketch, "E32.2.3.17", {"start": v(72.92, 86.11) * mm, "mid": v(74.08, 88.24) * mm, "end": v(72.92, 90.37) * mm});
            skLineSegment(sketch, "E32.2.3.18", {"start": v(72.92, 86.11) * mm, "end": v(64.88, 80.89) * mm});
            skArc(sketch, "E32.2.3.19", {"start": v(49.42, 68.84) * mm, "mid": v(50.8, 68.43) * mm, "end": v(52.18, 68.84) * mm});
            skArc(sketch, "E32.2.3.20", {"start": v(52.18, 83.56) * mm, "mid": v(50.8, 83.97) * mm, "end": v(49.42, 83.56) * mm});
            skLineSegment(sketch, "E32.2.3.21", {"start": v(54.08, 86.11) * mm, "end": v(62.12, 80.89) * mm});
            skLineSegment(sketch, "E32.2.3.22", {"start": v(52.18, 83.56) * mm, "end": v(60.22, 78.33) * mm});
            skArc(sketch, "E32.2.3.23", {"start": v(62.12, 80.89) * mm, "mid": v(63.5, 80.48) * mm, "end": v(64.88, 80.89) * mm});
            skPoint(sketch, "E32.3.0.0", {"position": v(101.6, 12.04) * mm});
            skPoint(sketch, "E32.3.0.1", {"position": v(88.9, 20.3) * mm});
            skPoint(sketch, "E32.3.0.2", {"position": v(76.2, 8.26) * mm});
            skPoint(sketch, "E32.3.0.3", {"position": v(63.5, 0) * mm});
            skPoint(sketch, "E32.3.0.4", {"position": v(76.2, -8.26) * mm});
            skPoint(sketch, "E32.3.0.5", {"position": v(88.9, 0) * mm});
            skPoint(sketch, "E32.3.0.6", {"position": v(76.2, 12.04) * mm});
            skPoint(sketch, "E32.3.0.7", {"position": v(88.9, 3.79) * mm});
            skArc(sketch, "E32.3.0.8", {"start": v(66.78, 2.13) * mm, "mid": v(65.62, 0) * mm, "end": v(66.78, -2.13) * mm});
            skLineSegment(sketch, "E32.3.0.9", {"start": v(90.28, 19.4) * mm, "end": v(98.32, 14.17) * mm});
            skArc(sketch, "E32.3.0.10", {"start": v(85.62, -2.13) * mm, "mid": v(86.78, 0) * mm, "end": v(85.62, 2.13) * mm});
            skArc(sketch, "E32.3.0.11", {"start": v(79.48, 14.17) * mm, "mid": v(78.32, 12.04) * mm, "end": v(79.48, 9.91) * mm});
            skLineSegment(sketch, "E32.3.0.12", {"start": v(79.48, 14.17) * mm, "end": v(87.52, 19.4) * mm});
            skLineSegment(sketch, "E32.3.0.13", {"start": v(85.62, -2.13) * mm, "end": v(77.58, -7.36) * mm});
            skLineSegment(sketch, "E32.3.0.14", {"start": v(74.82, -7.36) * mm, "end": v(66.78, -2.13) * mm});
            skLineSegment(sketch, "E32.3.0.15", {"start": v(66.78, 2.13) * mm, "end": v(74.82, 7.36) * mm});
            skArc(sketch, "E32.3.0.16", {"start": v(90.28, 19.4) * mm, "mid": v(88.9, 19.8) * mm, "end": v(87.52, 19.4) * mm});
            skArc(sketch, "E32.3.0.17", {"start": v(98.32, 9.91) * mm, "mid": v(99.48, 12.04) * mm, "end": v(98.32, 14.17) * mm});
            skLineSegment(sketch, "E32.3.0.18", {"start": v(98.32, 9.91) * mm, "end": v(90.28, 4.69) * mm});
            skArc(sketch, "E32.3.0.19", {"start": v(74.82, -7.36) * mm, "mid": v(76.2, -7.77) * mm, "end": v(77.58, -7.36) * mm});
            skArc(sketch, "E32.3.0.20", {"start": v(77.58, 7.36) * mm, "mid": v(76.2, 7.77) * mm, "end": v(74.82, 7.36) * mm});
            skLineSegment(sketch, "E32.3.0.21", {"start": v(79.48, 9.91) * mm, "end": v(87.52, 4.69) * mm});
            skLineSegment(sketch, "E32.3.0.22", {"start": v(77.58, 7.36) * mm, "end": v(85.62, 2.13) * mm});
            skArc(sketch, "E32.3.0.23", {"start": v(87.52, 4.69) * mm, "mid": v(88.9, 4.28) * mm, "end": v(90.28, 4.69) * mm});
            skPoint(sketch, "E32.3.1.0", {"position": v(101.6, 37.44) * mm});
            skPoint(sketch, "E32.3.1.1", {"position": v(88.9, 45.7) * mm});
            skPoint(sketch, "E32.3.1.2", {"position": v(76.2, 33.66) * mm});
            skPoint(sketch, "E32.3.1.3", {"position": v(63.5, 25.4) * mm});
            skPoint(sketch, "E32.3.1.4", {"position": v(76.2, 17.14) * mm});
            skPoint(sketch, "E32.3.1.5", {"position": v(88.9, 25.4) * mm});
            skPoint(sketch, "E32.3.1.6", {"position": v(76.2, 37.44) * mm});
            skPoint(sketch, "E32.3.1.7", {"position": v(88.9, 29.19) * mm});
            skArc(sketch, "E32.3.1.8", {"start": v(66.78, 27.53) * mm, "mid": v(65.62, 25.4) * mm, "end": v(66.78, 23.27) * mm});
            skLineSegment(sketch, "E32.3.1.9", {"start": v(90.28, 44.8) * mm, "end": v(98.32, 39.57) * mm});
            skArc(sketch, "E32.3.1.10", {"start": v(85.62, 23.27) * mm, "mid": v(86.78, 25.4) * mm, "end": v(85.62, 27.53) * mm});
            skArc(sketch, "E32.3.1.11", {"start": v(79.48, 39.57) * mm, "mid": v(78.32, 37.44) * mm, "end": v(79.48, 35.31) * mm});
            skLineSegment(sketch, "E32.3.1.12", {"start": v(79.48, 39.57) * mm, "end": v(87.52, 44.8) * mm});
            skLineSegment(sketch, "E32.3.1.13", {"start": v(85.62, 23.27) * mm, "end": v(77.58, 18.04) * mm});
            skLineSegment(sketch, "E32.3.1.14", {"start": v(74.82, 18.04) * mm, "end": v(66.78, 23.27) * mm});
            skLineSegment(sketch, "E32.3.1.15", {"start": v(66.78, 27.53) * mm, "end": v(74.82, 32.76) * mm});
            skArc(sketch, "E32.3.1.16", {"start": v(90.28, 44.8) * mm, "mid": v(88.9, 45.2) * mm, "end": v(87.52, 44.8) * mm});
            skArc(sketch, "E32.3.1.17", {"start": v(98.32, 35.31) * mm, "mid": v(99.48, 37.44) * mm, "end": v(98.32, 39.57) * mm});
            skLineSegment(sketch, "E32.3.1.18", {"start": v(98.32, 35.31) * mm, "end": v(90.28, 30.09) * mm});
            skArc(sketch, "E32.3.1.19", {"start": v(74.82, 18.04) * mm, "mid": v(76.2, 17.63) * mm, "end": v(77.58, 18.04) * mm});
            skArc(sketch, "E32.3.1.20", {"start": v(77.58, 32.76) * mm, "mid": v(76.2, 33.17) * mm, "end": v(74.82, 32.76) * mm});
            skLineSegment(sketch, "E32.3.1.21", {"start": v(79.48, 35.31) * mm, "end": v(87.52, 30.09) * mm});
            skLineSegment(sketch, "E32.3.1.22", {"start": v(77.58, 32.76) * mm, "end": v(85.62, 27.53) * mm});
            skArc(sketch, "E32.3.1.23", {"start": v(87.52, 30.09) * mm, "mid": v(88.9, 29.68) * mm, "end": v(90.28, 30.09) * mm});
            skPoint(sketch, "E32.3.2.0", {"position": v(101.6, 62.84) * mm});
            skPoint(sketch, "E32.3.2.1", {"position": v(88.9, 71.1) * mm});
            skPoint(sketch, "E32.3.2.2", {"position": v(76.2, 59.06) * mm});
            skPoint(sketch, "E32.3.2.3", {"position": v(63.5, 50.8) * mm});
            skPoint(sketch, "E32.3.2.4", {"position": v(76.2, 42.55) * mm});
            skPoint(sketch, "E32.3.2.5", {"position": v(88.9, 50.8) * mm});
            skPoint(sketch, "E32.3.2.6", {"position": v(76.2, 62.84) * mm});
            skPoint(sketch, "E32.3.2.7", {"position": v(88.9, 54.59) * mm});
            skArc(sketch, "E32.3.2.8", {"start": v(66.78, 52.93) * mm, "mid": v(65.62, 50.8) * mm, "end": v(66.78, 48.67) * mm});
            skLineSegment(sketch, "E32.3.2.9", {"start": v(90.28, 70.2) * mm, "end": v(98.32, 64.97) * mm});
            skArc(sketch, "E32.3.2.10", {"start": v(85.62, 48.67) * mm, "mid": v(86.78, 50.8) * mm, "end": v(85.62, 52.93) * mm});
            skArc(sketch, "E32.3.2.11", {"start": v(79.48, 64.97) * mm, "mid": v(78.32, 62.84) * mm, "end": v(79.48, 60.71) * mm});
            skLineSegment(sketch, "E32.3.2.12", {"start": v(79.48, 64.97) * mm, "end": v(87.52, 70.2) * mm});
            skLineSegment(sketch, "E32.3.2.13", {"start": v(85.62, 48.67) * mm, "end": v(77.58, 43.44) * mm});
            skLineSegment(sketch, "E32.3.2.14", {"start": v(74.82, 43.44) * mm, "end": v(66.78, 48.67) * mm});
            skLineSegment(sketch, "E32.3.2.15", {"start": v(66.78, 52.93) * mm, "end": v(74.82, 58.16) * mm});
            skArc(sketch, "E32.3.2.16", {"start": v(90.28, 70.2) * mm, "mid": v(88.9, 70.6) * mm, "end": v(87.52, 70.2) * mm});
            skArc(sketch, "E32.3.2.17", {"start": v(98.32, 60.71) * mm, "mid": v(99.48, 62.84) * mm, "end": v(98.32, 64.97) * mm});
            skLineSegment(sketch, "E32.3.2.18", {"start": v(98.32, 60.71) * mm, "end": v(90.28, 55.49) * mm});
            skArc(sketch, "E32.3.2.19", {"start": v(74.82, 43.44) * mm, "mid": v(76.2, 43.03) * mm, "end": v(77.58, 43.44) * mm});
            skArc(sketch, "E32.3.2.20", {"start": v(77.58, 58.16) * mm, "mid": v(76.2, 58.57) * mm, "end": v(74.82, 58.16) * mm});
            skLineSegment(sketch, "E32.3.2.21", {"start": v(79.48, 60.71) * mm, "end": v(87.52, 55.49) * mm});
            skLineSegment(sketch, "E32.3.2.22", {"start": v(77.58, 58.16) * mm, "end": v(85.62, 52.93) * mm});
            skArc(sketch, "E32.3.2.23", {"start": v(87.52, 55.49) * mm, "mid": v(88.9, 55.08) * mm, "end": v(90.28, 55.49) * mm});
            skPoint(sketch, "E32.3.3.0", {"position": v(101.6, 88.24) * mm});
            skPoint(sketch, "E32.3.3.1", {"position": v(88.9, 96.5) * mm});
            skPoint(sketch, "E32.3.3.2", {"position": v(76.2, 84.45) * mm});
            skPoint(sketch, "E32.3.3.3", {"position": v(63.5, 76.2) * mm});
            skPoint(sketch, "E32.3.3.4", {"position": v(76.2, 67.94) * mm});
            skPoint(sketch, "E32.3.3.5", {"position": v(88.9, 76.2) * mm});
            skPoint(sketch, "E32.3.3.6", {"position": v(76.2, 88.24) * mm});
            skPoint(sketch, "E32.3.3.7", {"position": v(88.9, 79.99) * mm});
            skArc(sketch, "E32.3.3.8", {"start": v(66.78, 78.33) * mm, "mid": v(65.62, 76.2) * mm, "end": v(66.78, 74.07) * mm});
            skLineSegment(sketch, "E32.3.3.9", {"start": v(90.28, 95.6) * mm, "end": v(98.32, 90.37) * mm});
            skArc(sketch, "E32.3.3.10", {"start": v(85.62, 74.07) * mm, "mid": v(86.78, 76.2) * mm, "end": v(85.62, 78.33) * mm});
            skArc(sketch, "E32.3.3.11", {"start": v(79.48, 90.37) * mm, "mid": v(78.32, 88.24) * mm, "end": v(79.48, 86.11) * mm});
            skLineSegment(sketch, "E32.3.3.12", {"start": v(79.48, 90.37) * mm, "end": v(87.52, 95.6) * mm});
            skLineSegment(sketch, "E32.3.3.13", {"start": v(85.62, 74.07) * mm, "end": v(77.58, 68.84) * mm});
            skLineSegment(sketch, "E32.3.3.14", {"start": v(74.82, 68.84) * mm, "end": v(66.78, 74.07) * mm});
            skLineSegment(sketch, "E32.3.3.15", {"start": v(66.78, 78.33) * mm, "end": v(74.82, 83.56) * mm});
            skArc(sketch, "E32.3.3.16", {"start": v(90.28, 95.6) * mm, "mid": v(88.9, 96) * mm, "end": v(87.52, 95.6) * mm});
            skArc(sketch, "E32.3.3.17", {"start": v(98.32, 86.11) * mm, "mid": v(99.48, 88.24) * mm, "end": v(98.32, 90.37) * mm});
            skLineSegment(sketch, "E32.3.3.18", {"start": v(98.32, 86.11) * mm, "end": v(90.28, 80.89) * mm});
            skArc(sketch, "E32.3.3.19", {"start": v(74.82, 68.84) * mm, "mid": v(76.2, 68.43) * mm, "end": v(77.58, 68.84) * mm});
            skArc(sketch, "E32.3.3.20", {"start": v(77.58, 83.56) * mm, "mid": v(76.2, 83.97) * mm, "end": v(74.82, 83.56) * mm});
            skLineSegment(sketch, "E32.3.3.21", {"start": v(79.48, 86.11) * mm, "end": v(87.52, 80.89) * mm});
            skLineSegment(sketch, "E32.3.3.22", {"start": v(77.58, 83.56) * mm, "end": v(85.62, 78.33) * mm});
            skArc(sketch, "E32.3.3.23", {"start": v(87.52, 80.89) * mm, "mid": v(88.9, 80.48) * mm, "end": v(90.28, 80.89) * mm});
            skPoint(sketch, "E32.4.0.0", {"position": v(127, 12.04) * mm});
            skPoint(sketch, "E32.4.0.1", {"position": v(114.3, 20.3) * mm});
            skPoint(sketch, "E32.4.0.2", {"position": v(101.6, 8.26) * mm});
            skPoint(sketch, "E32.4.0.3", {"position": v(88.9, 0) * mm});
            skPoint(sketch, "E32.4.0.4", {"position": v(101.6, -8.26) * mm});
            skPoint(sketch, "E32.4.0.5", {"position": v(114.3, 0) * mm});
            skPoint(sketch, "E32.4.0.6", {"position": v(101.6, 12.04) * mm});
            skPoint(sketch, "E32.4.0.7", {"position": v(114.3, 3.79) * mm});
            skArc(sketch, "E32.4.0.8", {"start": v(92.18, 2.13) * mm, "mid": v(91.02, 0) * mm, "end": v(92.18, -2.13) * mm});
            skLineSegment(sketch, "E32.4.0.9", {"start": v(115.68, 19.4) * mm, "end": v(123.72, 14.17) * mm});
            skArc(sketch, "E32.4.0.10", {"start": v(111.02, -2.13) * mm, "mid": v(112.18, 0) * mm, "end": v(111.02, 2.13) * mm});
            skArc(sketch, "E32.4.0.11", {"start": v(104.88, 14.17) * mm, "mid": v(103.72, 12.04) * mm, "end": v(104.88, 9.91) * mm});
            skLineSegment(sketch, "E32.4.0.12", {"start": v(104.88, 14.17) * mm, "end": v(112.92, 19.4) * mm});
            skLineSegment(sketch, "E32.4.0.13", {"start": v(111.02, -2.13) * mm, "end": v(102.98, -7.36) * mm});
            skLineSegment(sketch, "E32.4.0.14", {"start": v(100.22, -7.36) * mm, "end": v(92.18, -2.13) * mm});
            skLineSegment(sketch, "E32.4.0.15", {"start": v(92.18, 2.13) * mm, "end": v(100.22, 7.36) * mm});
            skArc(sketch, "E32.4.0.16", {"start": v(115.68, 19.4) * mm, "mid": v(114.3, 19.8) * mm, "end": v(112.92, 19.4) * mm});
            skArc(sketch, "E32.4.0.17", {"start": v(123.72, 9.91) * mm, "mid": v(124.88, 12.04) * mm, "end": v(123.72, 14.17) * mm});
            skLineSegment(sketch, "E32.4.0.18", {"start": v(123.72, 9.91) * mm, "end": v(115.68, 4.69) * mm});
            skArc(sketch, "E32.4.0.19", {"start": v(100.22, -7.36) * mm, "mid": v(101.6, -7.77) * mm, "end": v(102.98, -7.36) * mm});
            skArc(sketch, "E32.4.0.20", {"start": v(102.98, 7.36) * mm, "mid": v(101.6, 7.77) * mm, "end": v(100.22, 7.36) * mm});
            skLineSegment(sketch, "E32.4.0.21", {"start": v(104.88, 9.91) * mm, "end": v(112.92, 4.69) * mm});
            skLineSegment(sketch, "E32.4.0.22", {"start": v(102.98, 7.36) * mm, "end": v(111.02, 2.13) * mm});
            skArc(sketch, "E32.4.0.23", {"start": v(112.92, 4.69) * mm, "mid": v(114.3, 4.28) * mm, "end": v(115.68, 4.69) * mm});
            skPoint(sketch, "E32.4.1.0", {"position": v(127, 37.44) * mm});
            skPoint(sketch, "E32.4.1.1", {"position": v(114.3, 45.7) * mm});
            skPoint(sketch, "E32.4.1.2", {"position": v(101.6, 33.66) * mm});
            skPoint(sketch, "E32.4.1.3", {"position": v(88.9, 25.4) * mm});
            skPoint(sketch, "E32.4.1.4", {"position": v(101.6, 17.14) * mm});
            skPoint(sketch, "E32.4.1.5", {"position": v(114.3, 25.4) * mm});
            skPoint(sketch, "E32.4.1.6", {"position": v(101.6, 37.44) * mm});
            skPoint(sketch, "E32.4.1.7", {"position": v(114.3, 29.19) * mm});
            skArc(sketch, "E32.4.1.8", {"start": v(92.18, 27.53) * mm, "mid": v(91.02, 25.4) * mm, "end": v(92.18, 23.27) * mm});
            skLineSegment(sketch, "E32.4.1.9", {"start": v(115.68, 44.8) * mm, "end": v(123.72, 39.57) * mm});
            skArc(sketch, "E32.4.1.10", {"start": v(111.02, 23.27) * mm, "mid": v(112.18, 25.4) * mm, "end": v(111.02, 27.53) * mm});
            skArc(sketch, "E32.4.1.11", {"start": v(104.88, 39.57) * mm, "mid": v(103.72, 37.44) * mm, "end": v(104.88, 35.31) * mm});
            skLineSegment(sketch, "E32.4.1.12", {"start": v(104.88, 39.57) * mm, "end": v(112.92, 44.8) * mm});
            skLineSegment(sketch, "E32.4.1.13", {"start": v(111.02, 23.27) * mm, "end": v(102.98, 18.04) * mm});
            skLineSegment(sketch, "E32.4.1.14", {"start": v(100.22, 18.04) * mm, "end": v(92.18, 23.27) * mm});
            skLineSegment(sketch, "E32.4.1.15", {"start": v(92.18, 27.53) * mm, "end": v(100.22, 32.76) * mm});
            skArc(sketch, "E32.4.1.16", {"start": v(115.68, 44.8) * mm, "mid": v(114.3, 45.2) * mm, "end": v(112.92, 44.8) * mm});
            skArc(sketch, "E32.4.1.17", {"start": v(123.72, 35.31) * mm, "mid": v(124.88, 37.44) * mm, "end": v(123.72, 39.57) * mm});
            skLineSegment(sketch, "E32.4.1.18", {"start": v(123.72, 35.31) * mm, "end": v(115.68, 30.09) * mm});
            skArc(sketch, "E32.4.1.19", {"start": v(100.22, 18.04) * mm, "mid": v(101.6, 17.63) * mm, "end": v(102.98, 18.04) * mm});
            skArc(sketch, "E32.4.1.20", {"start": v(102.98, 32.76) * mm, "mid": v(101.6, 33.17) * mm, "end": v(100.22, 32.76) * mm});
            skLineSegment(sketch, "E32.4.1.21", {"start": v(104.88, 35.31) * mm, "end": v(112.92, 30.09) * mm});
            skLineSegment(sketch, "E32.4.1.22", {"start": v(102.98, 32.76) * mm, "end": v(111.02, 27.53) * mm});
            skArc(sketch, "E32.4.1.23", {"start": v(112.92, 30.09) * mm, "mid": v(114.3, 29.68) * mm, "end": v(115.68, 30.09) * mm});
            skPoint(sketch, "E32.4.2.0", {"position": v(127, 62.84) * mm});
            skPoint(sketch, "E32.4.2.1", {"position": v(114.3, 71.1) * mm});
            skPoint(sketch, "E32.4.2.2", {"position": v(101.6, 59.06) * mm});
            skPoint(sketch, "E32.4.2.3", {"position": v(88.9, 50.8) * mm});
            skPoint(sketch, "E32.4.2.4", {"position": v(101.6, 42.55) * mm});
            skPoint(sketch, "E32.4.2.5", {"position": v(114.3, 50.8) * mm});
            skPoint(sketch, "E32.4.2.6", {"position": v(101.6, 62.84) * mm});
            skPoint(sketch, "E32.4.2.7", {"position": v(114.3, 54.59) * mm});
            skArc(sketch, "E32.4.2.8", {"start": v(92.18, 52.93) * mm, "mid": v(91.02, 50.8) * mm, "end": v(92.18, 48.67) * mm});
            skLineSegment(sketch, "E32.4.2.9", {"start": v(115.68, 70.2) * mm, "end": v(123.72, 64.97) * mm});
            skArc(sketch, "E32.4.2.10", {"start": v(111.02, 48.67) * mm, "mid": v(112.18, 50.8) * mm, "end": v(111.02, 52.93) * mm});
            skArc(sketch, "E32.4.2.11", {"start": v(104.88, 64.97) * mm, "mid": v(103.72, 62.84) * mm, "end": v(104.88, 60.71) * mm});
            skLineSegment(sketch, "E32.4.2.12", {"start": v(104.88, 64.97) * mm, "end": v(112.92, 70.2) * mm});
            skLineSegment(sketch, "E32.4.2.13", {"start": v(111.02, 48.67) * mm, "end": v(102.98, 43.44) * mm});
            skLineSegment(sketch, "E32.4.2.14", {"start": v(100.22, 43.44) * mm, "end": v(92.18, 48.67) * mm});
            skLineSegment(sketch, "E32.4.2.15", {"start": v(92.18, 52.93) * mm, "end": v(100.22, 58.16) * mm});
            skArc(sketch, "E32.4.2.16", {"start": v(115.68, 70.2) * mm, "mid": v(114.3, 70.6) * mm, "end": v(112.92, 70.2) * mm});
            skArc(sketch, "E32.4.2.17", {"start": v(123.72, 60.71) * mm, "mid": v(124.88, 62.84) * mm, "end": v(123.72, 64.97) * mm});
            skLineSegment(sketch, "E32.4.2.18", {"start": v(123.72, 60.71) * mm, "end": v(115.68, 55.49) * mm});
            skArc(sketch, "E32.4.2.19", {"start": v(100.22, 43.44) * mm, "mid": v(101.6, 43.03) * mm, "end": v(102.98, 43.44) * mm});
            skArc(sketch, "E32.4.2.20", {"start": v(102.98, 58.16) * mm, "mid": v(101.6, 58.57) * mm, "end": v(100.22, 58.16) * mm});
            skLineSegment(sketch, "E32.4.2.21", {"start": v(104.88, 60.71) * mm, "end": v(112.92, 55.49) * mm});
            skLineSegment(sketch, "E32.4.2.22", {"start": v(102.98, 58.16) * mm, "end": v(111.02, 52.93) * mm});
            skArc(sketch, "E32.4.2.23", {"start": v(112.92, 55.49) * mm, "mid": v(114.3, 55.08) * mm, "end": v(115.68, 55.49) * mm});
            skPoint(sketch, "E32.4.3.0", {"position": v(127, 88.24) * mm});
            skPoint(sketch, "E32.4.3.1", {"position": v(114.3, 96.5) * mm});
            skPoint(sketch, "E32.4.3.2", {"position": v(101.6, 84.45) * mm});
            skPoint(sketch, "E32.4.3.3", {"position": v(88.9, 76.2) * mm});
            skPoint(sketch, "E32.4.3.4", {"position": v(101.6, 67.94) * mm});
            skPoint(sketch, "E32.4.3.5", {"position": v(114.3, 76.2) * mm});
            skPoint(sketch, "E32.4.3.6", {"position": v(101.6, 88.24) * mm});
            skPoint(sketch, "E32.4.3.7", {"position": v(114.3, 79.99) * mm});
            skArc(sketch, "E32.4.3.8", {"start": v(92.18, 78.33) * mm, "mid": v(91.02, 76.2) * mm, "end": v(92.18, 74.07) * mm});
            skLineSegment(sketch, "E32.4.3.9", {"start": v(115.68, 95.6) * mm, "end": v(123.72, 90.37) * mm});
            skArc(sketch, "E32.4.3.10", {"start": v(111.02, 74.07) * mm, "mid": v(112.18, 76.2) * mm, "end": v(111.02, 78.33) * mm});
            skArc(sketch, "E32.4.3.11", {"start": v(104.88, 90.37) * mm, "mid": v(103.72, 88.24) * mm, "end": v(104.88, 86.11) * mm});
            skLineSegment(sketch, "E32.4.3.12", {"start": v(104.88, 90.37) * mm, "end": v(112.92, 95.6) * mm});
            skLineSegment(sketch, "E32.4.3.13", {"start": v(111.02, 74.07) * mm, "end": v(102.98, 68.84) * mm});
            skLineSegment(sketch, "E32.4.3.14", {"start": v(100.22, 68.84) * mm, "end": v(92.18, 74.07) * mm});
            skLineSegment(sketch, "E32.4.3.15", {"start": v(92.18, 78.33) * mm, "end": v(100.22, 83.56) * mm});
            skArc(sketch, "E32.4.3.16", {"start": v(115.68, 95.6) * mm, "mid": v(114.3, 96) * mm, "end": v(112.92, 95.6) * mm});
            skArc(sketch, "E32.4.3.17", {"start": v(123.72, 86.11) * mm, "mid": v(124.88, 88.24) * mm, "end": v(123.72, 90.37) * mm});
            skLineSegment(sketch, "E32.4.3.18", {"start": v(123.72, 86.11) * mm, "end": v(115.68, 80.89) * mm});
            skArc(sketch, "E32.4.3.19", {"start": v(100.22, 68.84) * mm, "mid": v(101.6, 68.43) * mm, "end": v(102.98, 68.84) * mm});
            skArc(sketch, "E32.4.3.20", {"start": v(102.98, 83.56) * mm, "mid": v(101.6, 83.97) * mm, "end": v(100.22, 83.56) * mm});
            skLineSegment(sketch, "E32.4.3.21", {"start": v(104.88, 86.11) * mm, "end": v(112.92, 80.89) * mm});
            skLineSegment(sketch, "E32.4.3.22", {"start": v(102.98, 83.56) * mm, "end": v(111.02, 78.33) * mm});
            skArc(sketch, "E32.4.3.23", {"start": v(112.92, 80.89) * mm, "mid": v(114.3, 80.48) * mm, "end": v(115.68, 80.89) * mm});
            skPoint(sketch, "E32.5.0.0", {"position": v(152.4, 12.04) * mm});
            skPoint(sketch, "E32.5.0.1", {"position": v(139.7, 20.3) * mm});
            skPoint(sketch, "E32.5.0.2", {"position": v(127, 8.26) * mm});
            skPoint(sketch, "E32.5.0.3", {"position": v(114.3, 0) * mm});
            skPoint(sketch, "E32.5.0.4", {"position": v(127, -8.26) * mm});
            skPoint(sketch, "E32.5.0.5", {"position": v(139.7, 0) * mm});
            skPoint(sketch, "E32.5.0.6", {"position": v(127, 12.04) * mm});
            skPoint(sketch, "E32.5.0.7", {"position": v(139.7, 3.79) * mm});
            skArc(sketch, "E32.5.0.8", {"start": v(117.58, 2.13) * mm, "mid": v(116.42, 0) * mm, "end": v(117.58, -2.13) * mm});
            skLineSegment(sketch, "E32.5.0.9", {"start": v(141.08, 19.4) * mm, "end": v(149.12, 14.17) * mm});
            skArc(sketch, "E32.5.0.10", {"start": v(136.42, -2.13) * mm, "mid": v(137.58, 0) * mm, "end": v(136.42, 2.13) * mm});
            skArc(sketch, "E32.5.0.11", {"start": v(130.28, 14.17) * mm, "mid": v(129.12, 12.04) * mm, "end": v(130.28, 9.91) * mm});
            skLineSegment(sketch, "E32.5.0.12", {"start": v(130.28, 14.17) * mm, "end": v(138.32, 19.4) * mm});
            skLineSegment(sketch, "E32.5.0.13", {"start": v(136.42, -2.13) * mm, "end": v(128.38, -7.36) * mm});
            skLineSegment(sketch, "E32.5.0.14", {"start": v(125.62, -7.36) * mm, "end": v(117.58, -2.13) * mm});
            skLineSegment(sketch, "E32.5.0.15", {"start": v(117.58, 2.13) * mm, "end": v(125.62, 7.36) * mm});
            skArc(sketch, "E32.5.0.16", {"start": v(141.08, 19.4) * mm, "mid": v(139.7, 19.8) * mm, "end": v(138.32, 19.4) * mm});
            skArc(sketch, "E32.5.0.17", {"start": v(149.12, 9.91) * mm, "mid": v(150.28, 12.04) * mm, "end": v(149.12, 14.17) * mm});
            skLineSegment(sketch, "E32.5.0.18", {"start": v(149.12, 9.91) * mm, "end": v(141.08, 4.69) * mm});
            skArc(sketch, "E32.5.0.19", {"start": v(125.62, -7.36) * mm, "mid": v(127, -7.77) * mm, "end": v(128.38, -7.36) * mm});
            skArc(sketch, "E32.5.0.20", {"start": v(128.38, 7.36) * mm, "mid": v(127, 7.77) * mm, "end": v(125.62, 7.36) * mm});
            skLineSegment(sketch, "E32.5.0.21", {"start": v(130.28, 9.91) * mm, "end": v(138.32, 4.69) * mm});
            skLineSegment(sketch, "E32.5.0.22", {"start": v(128.38, 7.36) * mm, "end": v(136.42, 2.13) * mm});
            skArc(sketch, "E32.5.0.23", {"start": v(138.32, 4.69) * mm, "mid": v(139.7, 4.28) * mm, "end": v(141.08, 4.69) * mm});
            skPoint(sketch, "E32.5.1.0", {"position": v(152.4, 37.44) * mm});
            skPoint(sketch, "E32.5.1.1", {"position": v(139.7, 45.7) * mm});
            skPoint(sketch, "E32.5.1.2", {"position": v(127, 33.66) * mm});
            skPoint(sketch, "E32.5.1.3", {"position": v(114.3, 25.4) * mm});
            skPoint(sketch, "E32.5.1.4", {"position": v(127, 17.14) * mm});
            skPoint(sketch, "E32.5.1.5", {"position": v(139.7, 25.4) * mm});
            skPoint(sketch, "E32.5.1.6", {"position": v(127, 37.44) * mm});
            skPoint(sketch, "E32.5.1.7", {"position": v(139.7, 29.19) * mm});
            skArc(sketch, "E32.5.1.8", {"start": v(117.58, 27.53) * mm, "mid": v(116.42, 25.4) * mm, "end": v(117.58, 23.27) * mm});
            skLineSegment(sketch, "E32.5.1.9", {"start": v(141.08, 44.8) * mm, "end": v(149.12, 39.57) * mm});
            skArc(sketch, "E32.5.1.10", {"start": v(136.42, 23.27) * mm, "mid": v(137.58, 25.4) * mm, "end": v(136.42, 27.53) * mm});
            skArc(sketch, "E32.5.1.11", {"start": v(130.28, 39.57) * mm, "mid": v(129.12, 37.44) * mm, "end": v(130.28, 35.31) * mm});
            skLineSegment(sketch, "E32.5.1.12", {"start": v(130.28, 39.57) * mm, "end": v(138.32, 44.8) * mm});
            skLineSegment(sketch, "E32.5.1.13", {"start": v(136.42, 23.27) * mm, "end": v(128.38, 18.04) * mm});
            skLineSegment(sketch, "E32.5.1.14", {"start": v(125.62, 18.04) * mm, "end": v(117.58, 23.27) * mm});
            skLineSegment(sketch, "E32.5.1.15", {"start": v(117.58, 27.53) * mm, "end": v(125.62, 32.76) * mm});
            skArc(sketch, "E32.5.1.16", {"start": v(141.08, 44.8) * mm, "mid": v(139.7, 45.2) * mm, "end": v(138.32, 44.8) * mm});
            skArc(sketch, "E32.5.1.17", {"start": v(149.12, 35.31) * mm, "mid": v(150.28, 37.44) * mm, "end": v(149.12, 39.57) * mm});
            skLineSegment(sketch, "E32.5.1.18", {"start": v(149.12, 35.31) * mm, "end": v(141.08, 30.09) * mm});
            skArc(sketch, "E32.5.1.19", {"start": v(125.62, 18.04) * mm, "mid": v(127, 17.63) * mm, "end": v(128.38, 18.04) * mm});
            skArc(sketch, "E32.5.1.20", {"start": v(128.38, 32.76) * mm, "mid": v(127, 33.17) * mm, "end": v(125.62, 32.76) * mm});
            skLineSegment(sketch, "E32.5.1.21", {"start": v(130.28, 35.31) * mm, "end": v(138.32, 30.09) * mm});
            skLineSegment(sketch, "E32.5.1.22", {"start": v(128.38, 32.76) * mm, "end": v(136.42, 27.53) * mm});
            skArc(sketch, "E32.5.1.23", {"start": v(138.32, 30.09) * mm, "mid": v(139.7, 29.68) * mm, "end": v(141.08, 30.09) * mm});
            skPoint(sketch, "E32.5.2.0", {"position": v(152.4, 62.84) * mm});
            skPoint(sketch, "E32.5.2.1", {"position": v(139.7, 71.1) * mm});
            skPoint(sketch, "E32.5.2.2", {"position": v(127, 59.06) * mm});
            skPoint(sketch, "E32.5.2.3", {"position": v(114.3, 50.8) * mm});
            skPoint(sketch, "E32.5.2.4", {"position": v(127, 42.55) * mm});
            skPoint(sketch, "E32.5.2.5", {"position": v(139.7, 50.8) * mm});
            skPoint(sketch, "E32.5.2.6", {"position": v(127, 62.84) * mm});
            skPoint(sketch, "E32.5.2.7", {"position": v(139.7, 54.59) * mm});
            skArc(sketch, "E32.5.2.8", {"start": v(117.58, 52.93) * mm, "mid": v(116.42, 50.8) * mm, "end": v(117.58, 48.67) * mm});
            skLineSegment(sketch, "E32.5.2.9", {"start": v(141.08, 70.2) * mm, "end": v(149.12, 64.97) * mm});
            skArc(sketch, "E32.5.2.10", {"start": v(136.42, 48.67) * mm, "mid": v(137.58, 50.8) * mm, "end": v(136.42, 52.93) * mm});
            skArc(sketch, "E32.5.2.11", {"start": v(130.28, 64.97) * mm, "mid": v(129.12, 62.84) * mm, "end": v(130.28, 60.71) * mm});
            skLineSegment(sketch, "E32.5.2.12", {"start": v(130.28, 64.97) * mm, "end": v(138.32, 70.2) * mm});
            skLineSegment(sketch, "E32.5.2.13", {"start": v(136.42, 48.67) * mm, "end": v(128.38, 43.44) * mm});
            skLineSegment(sketch, "E32.5.2.14", {"start": v(125.62, 43.44) * mm, "end": v(117.58, 48.67) * mm});
            skLineSegment(sketch, "E32.5.2.15", {"start": v(117.58, 52.93) * mm, "end": v(125.62, 58.16) * mm});
            skArc(sketch, "E32.5.2.16", {"start": v(141.08, 70.2) * mm, "mid": v(139.7, 70.6) * mm, "end": v(138.32, 70.2) * mm});
            skArc(sketch, "E32.5.2.17", {"start": v(149.12, 60.71) * mm, "mid": v(150.28, 62.84) * mm, "end": v(149.12, 64.97) * mm});
            skLineSegment(sketch, "E32.5.2.18", {"start": v(149.12, 60.71) * mm, "end": v(141.08, 55.49) * mm});
            skArc(sketch, "E32.5.2.19", {"start": v(125.62, 43.44) * mm, "mid": v(127, 43.03) * mm, "end": v(128.38, 43.44) * mm});
            skArc(sketch, "E32.5.2.20", {"start": v(128.38, 58.16) * mm, "mid": v(127, 58.57) * mm, "end": v(125.62, 58.16) * mm});
            skLineSegment(sketch, "E32.5.2.21", {"start": v(130.28, 60.71) * mm, "end": v(138.32, 55.49) * mm});
            skLineSegment(sketch, "E32.5.2.22", {"start": v(128.38, 58.16) * mm, "end": v(136.42, 52.93) * mm});
            skArc(sketch, "E32.5.2.23", {"start": v(138.32, 55.49) * mm, "mid": v(139.7, 55.08) * mm, "end": v(141.08, 55.49) * mm});
            skPoint(sketch, "E32.5.3.0", {"position": v(152.4, 88.24) * mm});
            skPoint(sketch, "E32.5.3.1", {"position": v(139.7, 96.5) * mm});
            skPoint(sketch, "E32.5.3.2", {"position": v(127, 84.45) * mm});
            skPoint(sketch, "E32.5.3.3", {"position": v(114.3, 76.2) * mm});
            skPoint(sketch, "E32.5.3.4", {"position": v(127, 67.94) * mm});
            skPoint(sketch, "E32.5.3.5", {"position": v(139.7, 76.2) * mm});
            skPoint(sketch, "E32.5.3.6", {"position": v(127, 88.24) * mm});
            skPoint(sketch, "E32.5.3.7", {"position": v(139.7, 79.99) * mm});
            skArc(sketch, "E32.5.3.8", {"start": v(117.58, 78.33) * mm, "mid": v(116.42, 76.2) * mm, "end": v(117.58, 74.07) * mm});
            skLineSegment(sketch, "E32.5.3.9", {"start": v(141.08, 95.6) * mm, "end": v(149.12, 90.37) * mm});
            skArc(sketch, "E32.5.3.10", {"start": v(136.42, 74.07) * mm, "mid": v(137.58, 76.2) * mm, "end": v(136.42, 78.33) * mm});
            skArc(sketch, "E32.5.3.11", {"start": v(130.28, 90.37) * mm, "mid": v(129.12, 88.24) * mm, "end": v(130.28, 86.11) * mm});
            skLineSegment(sketch, "E32.5.3.12", {"start": v(130.28, 90.37) * mm, "end": v(138.32, 95.6) * mm});
            skLineSegment(sketch, "E32.5.3.13", {"start": v(136.42, 74.07) * mm, "end": v(128.38, 68.84) * mm});
            skLineSegment(sketch, "E32.5.3.14", {"start": v(125.62, 68.84) * mm, "end": v(117.58, 74.07) * mm});
            skLineSegment(sketch, "E32.5.3.15", {"start": v(117.58, 78.33) * mm, "end": v(125.62, 83.56) * mm});
            skArc(sketch, "E32.5.3.16", {"start": v(141.08, 95.6) * mm, "mid": v(139.7, 96) * mm, "end": v(138.32, 95.6) * mm});
            skArc(sketch, "E32.5.3.17", {"start": v(149.12, 86.11) * mm, "mid": v(150.28, 88.24) * mm, "end": v(149.12, 90.37) * mm});
            skLineSegment(sketch, "E32.5.3.18", {"start": v(149.12, 86.11) * mm, "end": v(141.08, 80.89) * mm});
            skArc(sketch, "E32.5.3.19", {"start": v(125.62, 68.84) * mm, "mid": v(127, 68.43) * mm, "end": v(128.38, 68.84) * mm});
            skArc(sketch, "E32.5.3.20", {"start": v(128.38, 83.56) * mm, "mid": v(127, 83.97) * mm, "end": v(125.62, 83.56) * mm});
            skLineSegment(sketch, "E32.5.3.21", {"start": v(130.28, 86.11) * mm, "end": v(138.32, 80.89) * mm});
            skLineSegment(sketch, "E32.5.3.22", {"start": v(128.38, 83.56) * mm, "end": v(136.42, 78.33) * mm});
            skArc(sketch, "E32.5.3.23", {"start": v(138.32, 80.89) * mm, "mid": v(139.7, 80.48) * mm, "end": v(141.08, 80.89) * mm});
            skPoint(sketch, "E32.6.0.0", {"position": v(177.8, 12.04) * mm});
            skPoint(sketch, "E32.6.0.1", {"position": v(165.1, 20.3) * mm});
            skPoint(sketch, "E32.6.0.2", {"position": v(152.4, 8.26) * mm});
            skPoint(sketch, "E32.6.0.3", {"position": v(139.7, 0) * mm});
            skPoint(sketch, "E32.6.0.4", {"position": v(152.4, -8.26) * mm});
            skPoint(sketch, "E32.6.0.5", {"position": v(165.1, 0) * mm});
            skPoint(sketch, "E32.6.0.6", {"position": v(152.4, 12.04) * mm});
            skPoint(sketch, "E32.6.0.7", {"position": v(165.1, 3.79) * mm});
            skArc(sketch, "E32.6.0.8", {"start": v(142.98, 2.13) * mm, "mid": v(141.82, 0) * mm, "end": v(142.98, -2.13) * mm});
            skLineSegment(sketch, "E32.6.0.9", {"start": v(166.48, 19.4) * mm, "end": v(174.52, 14.17) * mm});
            skArc(sketch, "E32.6.0.10", {"start": v(161.82, -2.13) * mm, "mid": v(162.98, 0) * mm, "end": v(161.82, 2.13) * mm});
            skArc(sketch, "E32.6.0.11", {"start": v(155.68, 14.17) * mm, "mid": v(154.52, 12.04) * mm, "end": v(155.68, 9.91) * mm});
            skLineSegment(sketch, "E32.6.0.12", {"start": v(155.68, 14.17) * mm, "end": v(163.72, 19.4) * mm});
            skLineSegment(sketch, "E32.6.0.13", {"start": v(161.82, -2.13) * mm, "end": v(153.78, -7.36) * mm});
            skLineSegment(sketch, "E32.6.0.14", {"start": v(151.02, -7.36) * mm, "end": v(142.98, -2.13) * mm});
            skLineSegment(sketch, "E32.6.0.15", {"start": v(142.98, 2.13) * mm, "end": v(151.02, 7.36) * mm});
            skArc(sketch, "E32.6.0.16", {"start": v(166.48, 19.4) * mm, "mid": v(165.1, 19.8) * mm, "end": v(163.72, 19.4) * mm});
            skArc(sketch, "E32.6.0.17", {"start": v(174.52, 9.91) * mm, "mid": v(175.68, 12.04) * mm, "end": v(174.52, 14.17) * mm});
            skLineSegment(sketch, "E32.6.0.18", {"start": v(174.52, 9.91) * mm, "end": v(166.48, 4.69) * mm});
            skArc(sketch, "E32.6.0.19", {"start": v(151.02, -7.36) * mm, "mid": v(152.4, -7.77) * mm, "end": v(153.78, -7.36) * mm});
            skArc(sketch, "E32.6.0.20", {"start": v(153.78, 7.36) * mm, "mid": v(152.4, 7.77) * mm, "end": v(151.02, 7.36) * mm});
            skLineSegment(sketch, "E32.6.0.21", {"start": v(155.68, 9.91) * mm, "end": v(163.72, 4.69) * mm});
            skLineSegment(sketch, "E32.6.0.22", {"start": v(153.78, 7.36) * mm, "end": v(161.82, 2.13) * mm});
            skArc(sketch, "E32.6.0.23", {"start": v(163.72, 4.69) * mm, "mid": v(165.1, 4.28) * mm, "end": v(166.48, 4.69) * mm});
            skPoint(sketch, "E32.6.1.0", {"position": v(177.8, 37.44) * mm});
            skPoint(sketch, "E32.6.1.1", {"position": v(165.1, 45.7) * mm});
            skPoint(sketch, "E32.6.1.2", {"position": v(152.4, 33.66) * mm});
            skPoint(sketch, "E32.6.1.3", {"position": v(139.7, 25.4) * mm});
            skPoint(sketch, "E32.6.1.4", {"position": v(152.4, 17.14) * mm});
            skPoint(sketch, "E32.6.1.5", {"position": v(165.1, 25.4) * mm});
            skPoint(sketch, "E32.6.1.6", {"position": v(152.4, 37.44) * mm});
            skPoint(sketch, "E32.6.1.7", {"position": v(165.1, 29.19) * mm});
            skArc(sketch, "E32.6.1.8", {"start": v(142.98, 27.53) * mm, "mid": v(141.82, 25.4) * mm, "end": v(142.98, 23.27) * mm});
            skLineSegment(sketch, "E32.6.1.9", {"start": v(166.48, 44.8) * mm, "end": v(174.52, 39.57) * mm});
            skArc(sketch, "E32.6.1.10", {"start": v(161.82, 23.27) * mm, "mid": v(162.98, 25.4) * mm, "end": v(161.82, 27.53) * mm});
            skArc(sketch, "E32.6.1.11", {"start": v(155.68, 39.57) * mm, "mid": v(154.52, 37.44) * mm, "end": v(155.68, 35.31) * mm});
            skLineSegment(sketch, "E32.6.1.12", {"start": v(155.68, 39.57) * mm, "end": v(163.72, 44.8) * mm});
            skLineSegment(sketch, "E32.6.1.13", {"start": v(161.82, 23.27) * mm, "end": v(153.78, 18.04) * mm});
            skLineSegment(sketch, "E32.6.1.14", {"start": v(151.02, 18.04) * mm, "end": v(142.98, 23.27) * mm});
            skLineSegment(sketch, "E32.6.1.15", {"start": v(142.98, 27.53) * mm, "end": v(151.02, 32.76) * mm});
            skArc(sketch, "E32.6.1.16", {"start": v(166.48, 44.8) * mm, "mid": v(165.1, 45.2) * mm, "end": v(163.72, 44.8) * mm});
            skArc(sketch, "E32.6.1.17", {"start": v(174.52, 35.31) * mm, "mid": v(175.68, 37.44) * mm, "end": v(174.52, 39.57) * mm});
            skLineSegment(sketch, "E32.6.1.18", {"start": v(174.52, 35.31) * mm, "end": v(166.48, 30.09) * mm});
            skArc(sketch, "E32.6.1.19", {"start": v(151.02, 18.04) * mm, "mid": v(152.4, 17.63) * mm, "end": v(153.78, 18.04) * mm});
            skArc(sketch, "E32.6.1.20", {"start": v(153.78, 32.76) * mm, "mid": v(152.4, 33.17) * mm, "end": v(151.02, 32.76) * mm});
            skLineSegment(sketch, "E32.6.1.21", {"start": v(155.68, 35.31) * mm, "end": v(163.72, 30.09) * mm});
            skLineSegment(sketch, "E32.6.1.22", {"start": v(153.78, 32.76) * mm, "end": v(161.82, 27.53) * mm});
            skArc(sketch, "E32.6.1.23", {"start": v(163.72, 30.09) * mm, "mid": v(165.1, 29.68) * mm, "end": v(166.48, 30.09) * mm});
            skPoint(sketch, "E32.6.2.0", {"position": v(177.8, 62.84) * mm});
            skPoint(sketch, "E32.6.2.1", {"position": v(165.1, 71.1) * mm});
            skPoint(sketch, "E32.6.2.2", {"position": v(152.4, 59.06) * mm});
            skPoint(sketch, "E32.6.2.3", {"position": v(139.7, 50.8) * mm});
            skPoint(sketch, "E32.6.2.4", {"position": v(152.4, 42.55) * mm});
            skPoint(sketch, "E32.6.2.5", {"position": v(165.1, 50.8) * mm});
            skPoint(sketch, "E32.6.2.6", {"position": v(152.4, 62.84) * mm});
            skPoint(sketch, "E32.6.2.7", {"position": v(165.1, 54.59) * mm});
            skArc(sketch, "E32.6.2.8", {"start": v(142.98, 52.93) * mm, "mid": v(141.82, 50.8) * mm, "end": v(142.98, 48.67) * mm});
            skLineSegment(sketch, "E32.6.2.9", {"start": v(166.48, 70.2) * mm, "end": v(174.52, 64.97) * mm});
            skArc(sketch, "E32.6.2.10", {"start": v(161.82, 48.67) * mm, "mid": v(162.98, 50.8) * mm, "end": v(161.82, 52.93) * mm});
            skArc(sketch, "E32.6.2.11", {"start": v(155.68, 64.97) * mm, "mid": v(154.52, 62.84) * mm, "end": v(155.68, 60.71) * mm});
            skLineSegment(sketch, "E32.6.2.12", {"start": v(155.68, 64.97) * mm, "end": v(163.72, 70.2) * mm});
            skLineSegment(sketch, "E32.6.2.13", {"start": v(161.82, 48.67) * mm, "end": v(153.78, 43.44) * mm});
            skLineSegment(sketch, "E32.6.2.14", {"start": v(151.02, 43.44) * mm, "end": v(142.98, 48.67) * mm});
            skLineSegment(sketch, "E32.6.2.15", {"start": v(142.98, 52.93) * mm, "end": v(151.02, 58.16) * mm});
            skArc(sketch, "E32.6.2.16", {"start": v(166.48, 70.2) * mm, "mid": v(165.1, 70.6) * mm, "end": v(163.72, 70.2) * mm});
            skArc(sketch, "E32.6.2.17", {"start": v(174.52, 60.71) * mm, "mid": v(175.68, 62.84) * mm, "end": v(174.52, 64.97) * mm});
            skLineSegment(sketch, "E32.6.2.18", {"start": v(174.52, 60.71) * mm, "end": v(166.48, 55.49) * mm});
            skArc(sketch, "E32.6.2.19", {"start": v(151.02, 43.44) * mm, "mid": v(152.4, 43.03) * mm, "end": v(153.78, 43.44) * mm});
            skArc(sketch, "E32.6.2.20", {"start": v(153.78, 58.16) * mm, "mid": v(152.4, 58.57) * mm, "end": v(151.02, 58.16) * mm});
            skLineSegment(sketch, "E32.6.2.21", {"start": v(155.68, 60.71) * mm, "end": v(163.72, 55.49) * mm});
            skLineSegment(sketch, "E32.6.2.22", {"start": v(153.78, 58.16) * mm, "end": v(161.82, 52.93) * mm});
            skArc(sketch, "E32.6.2.23", {"start": v(163.72, 55.49) * mm, "mid": v(165.1, 55.08) * mm, "end": v(166.48, 55.49) * mm});
            skPoint(sketch, "E32.6.3.0", {"position": v(177.8, 88.24) * mm});
            skPoint(sketch, "E32.6.3.1", {"position": v(165.1, 96.5) * mm});
            skPoint(sketch, "E32.6.3.2", {"position": v(152.4, 84.45) * mm});
            skPoint(sketch, "E32.6.3.3", {"position": v(139.7, 76.2) * mm});
            skPoint(sketch, "E32.6.3.4", {"position": v(152.4, 67.94) * mm});
            skPoint(sketch, "E32.6.3.5", {"position": v(165.1, 76.2) * mm});
            skPoint(sketch, "E32.6.3.6", {"position": v(152.4, 88.24) * mm});
            skPoint(sketch, "E32.6.3.7", {"position": v(165.1, 79.99) * mm});
            skArc(sketch, "E32.6.3.8", {"start": v(142.98, 78.33) * mm, "mid": v(141.82, 76.2) * mm, "end": v(142.98, 74.07) * mm});
            skLineSegment(sketch, "E32.6.3.9", {"start": v(166.48, 95.6) * mm, "end": v(174.52, 90.37) * mm});
            skArc(sketch, "E32.6.3.10", {"start": v(161.82, 74.07) * mm, "mid": v(162.98, 76.2) * mm, "end": v(161.82, 78.33) * mm});
            skArc(sketch, "E32.6.3.11", {"start": v(155.68, 90.37) * mm, "mid": v(154.52, 88.24) * mm, "end": v(155.68, 86.11) * mm});
            skLineSegment(sketch, "E32.6.3.12", {"start": v(155.68, 90.37) * mm, "end": v(163.72, 95.6) * mm});
            skLineSegment(sketch, "E32.6.3.13", {"start": v(161.82, 74.07) * mm, "end": v(153.78, 68.84) * mm});
            skLineSegment(sketch, "E32.6.3.14", {"start": v(151.02, 68.84) * mm, "end": v(142.98, 74.07) * mm});
            skLineSegment(sketch, "E32.6.3.15", {"start": v(142.98, 78.33) * mm, "end": v(151.02, 83.56) * mm});
            skArc(sketch, "E32.6.3.16", {"start": v(166.48, 95.6) * mm, "mid": v(165.1, 96) * mm, "end": v(163.72, 95.6) * mm});
            skArc(sketch, "E32.6.3.17", {"start": v(174.52, 86.11) * mm, "mid": v(175.68, 88.24) * mm, "end": v(174.52, 90.37) * mm});
            skLineSegment(sketch, "E32.6.3.18", {"start": v(174.52, 86.11) * mm, "end": v(166.48, 80.89) * mm});
            skArc(sketch, "E32.6.3.19", {"start": v(151.02, 68.84) * mm, "mid": v(152.4, 68.43) * mm, "end": v(153.78, 68.84) * mm});
            skArc(sketch, "E32.6.3.20", {"start": v(153.78, 83.56) * mm, "mid": v(152.4, 83.97) * mm, "end": v(151.02, 83.56) * mm});
            skLineSegment(sketch, "E32.6.3.21", {"start": v(155.68, 86.11) * mm, "end": v(163.72, 80.89) * mm});
            skLineSegment(sketch, "E32.6.3.22", {"start": v(153.78, 83.56) * mm, "end": v(161.82, 78.33) * mm});
            skArc(sketch, "E32.6.3.23", {"start": v(163.72, 80.89) * mm, "mid": v(165.1, 80.48) * mm, "end": v(166.48, 80.89) * mm});
            skLineSegment(sketch, "E32.direction1", {"start": v(-12.7, 0) * mm, "end": v(12.7, 0) * mm, "construction": true});
            skLineSegment(sketch, "E32.direction2", {"start": v(-12.7, 0) * mm, "end": v(-12.7, 25.4) * mm, "construction": true});
            skSolve(sketch);
        }
        {
            var Q0;
            Q0=qSketchRegion(id+"F5",true);
            extrude(context, id + "F6", {"entities" : qUnion([Q0]), "operationType" : NewBodyOperationType.REMOVE, "oppositeDirection" : true, "depth" : 25.4 * mm});
        }
    });
